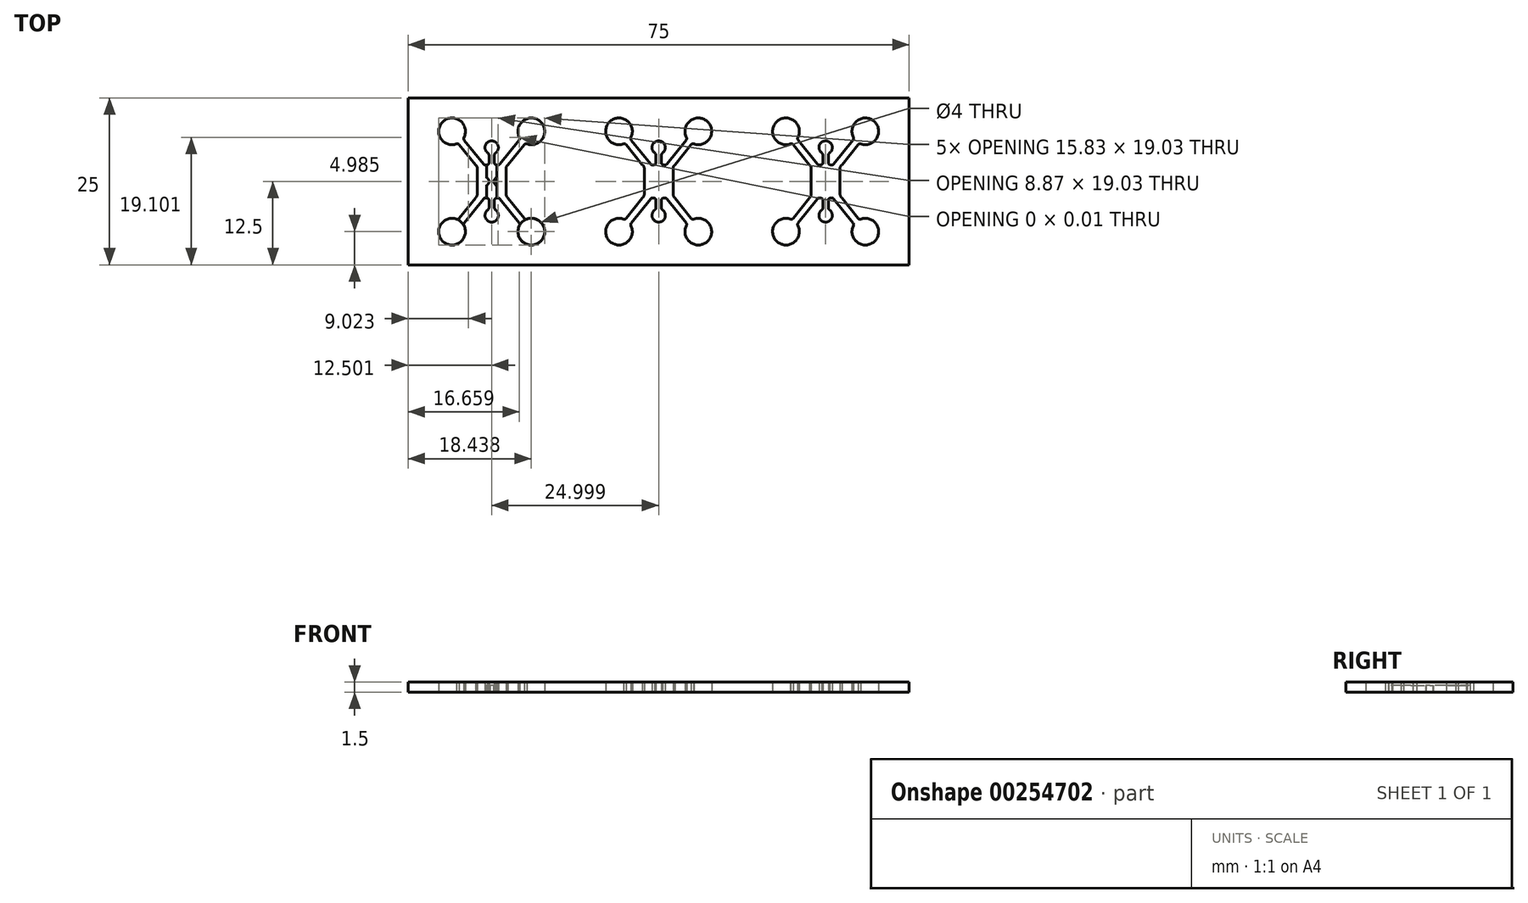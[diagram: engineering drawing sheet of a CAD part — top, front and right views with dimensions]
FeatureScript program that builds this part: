
annotation { "Feature Type Name" : "Feature", "Feature Type Description" : "" }
export const myFeature = defineFeature(function(context is Context, id is Id, definition is map)
    precondition{}
    {
        {
            var Q0;
            Q0=qCreatedBy(makeId("Top.planeOp"),FACE);
            var sketch = newSketch(context, id + "F0", { "sketchPlane" : qUnion([Q0])});
            skLineSegment(sketch, "E0.bottom", {"start": v(-37.5, 40) * mm, "end": v(37.5, 40) * mm});
            skLineSegment(sketch, "E0.top", {"start": v(-37.5, 15) * mm, "end": v(37.5, 15) * mm});
            skLineSegment(sketch, "E0.left", {"start": v(-37.5, 40) * mm, "end": v(-37.5, 15) * mm});
            skLineSegment(sketch, "E1.0", {"start": v(-37.5, 12.5) * mm, "end": v(37.5, 12.5) * mm});
            skLineSegment(sketch, "E2.top", {"start": v(-37.5, -12.5) * mm, "end": v(37.5, -12.5) * mm});
            skLineSegment(sketch, "E2.left", {"start": v(-37.5, 12.5) * mm, "end": v(-37.5, -12.5) * mm});
            skLineSegment(sketch, "E2.right", {"start": v(37.5, 12.5) * mm, "end": v(37.5, -12.5) * mm});
            skPoint(sketch, "E3.1.0.0", {"position": v(-17.06, 20.06) * mm});
            skPoint(sketch, "E3.1.0.4", {"position": v(-14.85, 26.8) * mm});
            skPoint(sketch, "E3.1.0.5", {"position": v(-25, 21.41) * mm});
            skLineSegment(sketch, "E3.1.0.10", {"start": v(-27.42, 30) * mm, "end": v(-29.86, 33.04) * mm});
            skPoint(sketch, "E3.1.0.11", {"position": v(-32.94, 20.06) * mm});
            skPoint(sketch, "E3.1.0.13", {"position": v(-25.75, 25) * mm});
            skPoint(sketch, "E3.1.0.15", {"position": v(-17.06, 34.94) * mm});
            skPoint(sketch, "E3.1.0.16", {"position": v(-24.49, 21.55) * mm});
            skLineSegment(sketch, "E3.1.0.17", {"start": v(-26.21, 24.92) * mm, "end": v(-29.12, 21.3) * mm});
            skLineSegment(sketch, "E3.1.0.19", {"start": v(-26.21, 30.08) * mm, "end": v(-29.1, 33.69) * mm});
            skLineSegment(sketch, "E3.1.0.20", {"start": v(-27.42, 25) * mm, "end": v(-29.87, 21.96) * mm});
            skPoint(sketch, "E3.1.0.24", {"position": v(-20.15, 29.65) * mm});
            skPoint(sketch, "E3.1.0.25", {"position": v(-22.85, 25.35) * mm});
            skPoint(sketch, "E3.1.0.27", {"position": v(-35.15, 26.8) * mm});
            skPoint(sketch, "E3.1.0.31", {"position": v(-27.15, 29.65) * mm});
            skPoint(sketch, "E3.1.0.35", {"position": v(-25.75, 30) * mm});
            skPoint(sketch, "E3.1.0.36", {"position": v(-27.15, 25.35) * mm});
            skPoint(sketch, "E3.1.0.41", {"position": v(-32.94, 34.94) * mm});
            skLineSegment(sketch, "E3.1.0.42", {"start": v(-23.79, 30.08) * mm, "end": v(-20.88, 33.7) * mm});
            skArc(sketch, "E3.1.0.43", {"start": v(-29.91, 29.7) * mm, "mid": v(-30, 29.78) * mm, "end": v(-30.1, 29.86) * mm});
            skArc(sketch, "E3.1.0.44", {"start": v(-20.08, 25.27) * mm, "mid": v(-14.77, 27.37) * mm, "end": v(-19.9, 29.89) * mm});
            skCircle(sketch, "E3.1.0.45", {"center": v(-19.06, 19.98) * mm, "radius": 2 * mm});
            skLineSegment(sketch, "E3.1.0.46", {"start": v(-23.79, 24.92) * mm, "end": v(-20.88, 21.3) * mm});
            skCircle(sketch, "E3.1.0.47", {"center": v(-30.94, 19.98) * mm, "radius": 2 * mm});
            skPoint(sketch, "E3.1.0.50", {"position": v(-25, 33.59) * mm});
            skLineSegment(sketch, "E3.1.0.60", {"start": v(-22.58, 25) * mm, "end": v(-20.13, 21.96) * mm});
            skPoint(sketch, "E3.1.0.61", {"position": v(-27.15, 25.35) * mm});
            skPoint(sketch, "E3.1.0.62", {"position": v(-27.15, 29.65) * mm});
            skPoint(sketch, "E3.1.0.64", {"position": v(-22.85, 25.35) * mm});
            skLineSegment(sketch, "E3.1.0.68", {"start": v(-22.58, 30) * mm, "end": v(-20.14, 33.04) * mm});
            skPoint(sketch, "E3.1.0.69", {"position": v(-27.15, 25.35) * mm});
            skPoint(sketch, "E3.1.0.72", {"position": v(-27.15, 29.65) * mm});
            skLineSegment(sketch, "E3.1.0.78", {"start": v(-29.85, 29.65) * mm, "end": v(-29.86, 29.65) * mm});
            skPoint(sketch, "E3.1.0.79", {"position": v(-22.85, 29.65) * mm});
            skPoint(sketch, "E3.1.0.81", {"position": v(-22.85, 25.35) * mm});
            skPoint(sketch, "E3.1.0.85", {"position": v(-22.85, 25.35) * mm});
            skPoint(sketch, "E3.1.0.87", {"position": v(-27.15, 25.35) * mm});
            skPoint(sketch, "E3.1.0.88", {"position": v(-27.15, 29.65) * mm});
            skLineSegment(sketch, "E3.1.0.89", {"start": v(-22.15, 29.65) * mm, "end": v(-20.49, 29.65) * mm});
            skPoint(sketch, "E3.1.0.90", {"position": v(-25, 27.5) * mm});
            skPoint(sketch, "E3.1.0.92", {"position": v(-22.85, 29.65) * mm});
            skPoint(sketch, "E3.1.0.95", {"position": v(-22.85, 25.35) * mm});
            skPoint(sketch, "E3.1.0.98", {"position": v(-27.15, 29.65) * mm});
            skPoint(sketch, "E3.1.0.99", {"position": v(-27.15, 25.35) * mm});
            skPoint(sketch, "E3.1.0.100", {"position": v(-22.85, 29.65) * mm});
            skLineSegment(sketch, "E3.1.0.104", {"start": v(-25.75, 25.21) * mm, "end": v(-25.75, 29.79) * mm});
            skLineSegment(sketch, "E3.1.0.105", {"start": v(-24.25, 29.79) * mm, "end": v(-24.25, 28.19) * mm});
            skLineSegment(sketch, "E3.1.0.106", {"start": v(-24.6, 24.7) * mm, "end": v(-24.6, 23.58) * mm});
            skLineSegment(sketch, "E3.1.0.108", {"start": v(-22.41, 29.65) * mm, "end": v(-22.15, 29.65) * mm});
            skLineSegment(sketch, "E3.1.0.109", {"start": v(-24.04, 30) * mm, "end": v(-23.95, 30) * mm});
            skLineSegment(sketch, "E3.1.0.110", {"start": v(-25.4, 30.5) * mm, "end": v(-25.4, 30.3) * mm});
            skArc(sketch, "E3.1.0.111", {"start": v(-24.6, 30.3) * mm, "mid": v(-24.51, 30.09) * mm, "end": v(-24.3, 30) * mm});
            skArc(sketch, "E3.1.0.112", {"start": v(-25.4, 30.3) * mm, "mid": v(-25.49, 30.09) * mm, "end": v(-25.7, 30) * mm});
            skLineSegment(sketch, "E3.1.0.113", {"start": v(-24.6, 30.3) * mm, "end": v(-24.6, 31.42) * mm});
            skLineSegment(sketch, "E3.1.0.115", {"start": v(-24.25, 30) * mm, "end": v(-24.3, 30) * mm});
            skLineSegment(sketch, "E3.1.0.117", {"start": v(-25.96, 30) * mm, "end": v(-26.05, 30) * mm});
            skLineSegment(sketch, "E3.1.0.118", {"start": v(-25.4, 24.7) * mm, "end": v(-25.4, 24.5) * mm});
            skLineSegment(sketch, "E3.1.0.120", {"start": v(-25.96, 25) * mm, "end": v(-26.05, 25) * mm});
            skArc(sketch, "E3.1.0.123", {"start": v(-25.4, 24.7) * mm, "mid": v(-25.49, 24.91) * mm, "end": v(-25.7, 25) * mm});
            skLineSegment(sketch, "E3.1.0.125", {"start": v(-24.25, 25) * mm, "end": v(-24.3, 25) * mm});
            skLineSegment(sketch, "E3.1.0.128", {"start": v(-24.04, 25) * mm, "end": v(-23.95, 25) * mm});
            skArc(sketch, "E3.1.0.134", {"start": v(-24.6, 24.7) * mm, "mid": v(-24.51, 24.91) * mm, "end": v(-24.3, 25) * mm});
            skLineSegment(sketch, "E3.1.0.151", {"start": v(-27.59, 25.35) * mm, "end": v(-27.85, 25.35) * mm});
            skLineSegment(sketch, "E4", {"start": v(-25.4, 24.5) * mm, "end": v(-25.4, 23.58) * mm});
            skLineSegment(sketch, "E5.top", {"start": v(-22.41, 25.35) * mm, "end": v(-20.5, 25.35) * mm});
            skLineSegment(sketch, "E5.left", {"start": v(-22.85, 29.44) * mm, "end": v(-22.85, 25.56) * mm});
            skLineSegment(sketch, "E5.right", {"start": v(-20.15, 29.57) * mm, "end": v(-20.15, 25.42) * mm});
            skLineSegment(sketch, "E6.right", {"start": v(-27.15, 29.44) * mm, "end": v(-27.15, 25.56) * mm});
            skLineSegment(sketch, "E7", {"start": v(-25.75, 25) * mm, "end": v(-25.7, 25) * mm});
            skLineSegment(sketch, "E8", {"start": v(-25.75, 30) * mm, "end": v(-25.7, 30) * mm});
            skLineSegment(sketch, "E9", {"start": v(-29.85, 25.35) * mm, "end": v(-29.85, 25.34) * mm});
            skArc(sketch, "E10.filletArc", {"start": v(-22.41, 25.35) * mm, "mid": v(-22.6, 25.23) * mm, "end": v(-22.58, 25) * mm});
            skPoint(sketch, "E11.visualSharp", {"position": v(-23.85, 25) * mm});
            skArc(sketch, "E11.filletArc", {"start": v(-23.79, 24.92) * mm, "mid": v(-23.86, 24.98) * mm, "end": v(-23.95, 25) * mm});
            skArc(sketch, "E12.filletArc", {"start": v(-22.58, 30) * mm, "mid": v(-22.6, 29.77) * mm, "end": v(-22.41, 29.65) * mm});
            skPoint(sketch, "E13.visualSharp", {"position": v(-23.85, 30) * mm});
            skArc(sketch, "E13.filletArc", {"start": v(-23.95, 30) * mm, "mid": v(-23.86, 30.02) * mm, "end": v(-23.79, 30.08) * mm});
            skPoint(sketch, "E14.visualSharp", {"position": v(-26.15, 30) * mm});
            skArc(sketch, "E14.filletArc", {"start": v(-26.21, 30.08) * mm, "mid": v(-26.14, 30.02) * mm, "end": v(-26.05, 30) * mm});
            skPoint(sketch, "E15.visualSharp", {"position": v(-26.15, 25) * mm});
            skArc(sketch, "E15.filletArc", {"start": v(-26.05, 25) * mm, "mid": v(-26.14, 24.98) * mm, "end": v(-26.21, 24.92) * mm});
            skArc(sketch, "E16", {"start": v(-27.42, 25) * mm, "mid": v(-27.26, 25.27) * mm, "end": v(-27.15, 25.56) * mm});
            skArc(sketch, "E17", {"start": v(-27.15, 29.44) * mm, "mid": v(-27.22, 29.75) * mm, "end": v(-27.42, 30) * mm});
            skArc(sketch, "E18", {"start": v(-27.59, 29.65) * mm, "mid": v(-27.43, 29.78) * mm, "end": v(-27.42, 30) * mm});
            skArc(sketch, "E19", {"start": v(-27.42, 25) * mm, "mid": v(-27.4, 25.23) * mm, "end": v(-27.59, 25.35) * mm});
            skArc(sketch, "E20.MirrorCS", {"start": v(-22.58, 25) * mm, "mid": v(-22.6, 25.23) * mm, "end": v(-22.41, 25.35) * mm});
            skArc(sketch, "E21.MirrorCS", {"start": v(-22.85, 29.44) * mm, "mid": v(-22.78, 29.75) * mm, "end": v(-22.58, 30) * mm});
            skArc(sketch, "E22.MirrorCS", {"start": v(-22.58, 25) * mm, "mid": v(-22.74, 25.27) * mm, "end": v(-22.85, 25.56) * mm});
            skLineSegment(sketch, "E23", {"start": v(-22.41, 29.65) * mm, "end": v(-20.49, 29.65) * mm});
            skArc(sketch, "E24", {"start": v(-19.9, 25.1) * mm, "mid": v(-20.18, 25.26) * mm, "end": v(-20.5, 25.35) * mm});
            skArc(sketch, "E25", {"start": v(-20.13, 21.96) * mm, "mid": v(-19.95, 21.86) * mm, "end": v(-19.75, 21.86) * mm});
            skArc(sketch, "E26", {"start": v(-20.85, 20.88) * mm, "mid": v(-20.81, 21.1) * mm, "end": v(-20.88, 21.3) * mm});
            skLineSegment(sketch, "E27", {"start": v(-24.6, 23.58) * mm, "end": v(-24.6, 23.58) * mm});
            skArc(sketch, "E28.MirrorCS", {"start": v(-29.87, 21.96) * mm, "mid": v(-30.05, 21.86) * mm, "end": v(-30.25, 21.86) * mm});
            skArc(sketch, "E29.MirrorCS", {"start": v(-29.15, 20.88) * mm, "mid": v(-29.19, 21.1) * mm, "end": v(-29.12, 21.3) * mm});
            skArc(sketch, "E30.MirrorCS", {"start": v(-25.4, 23.58) * mm, "mid": v(-25.46, 23.37) * mm, "end": v(-25.61, 23.2) * mm});
            skArc(sketch, "E31", {"start": v(-24.6, 23.58) * mm, "mid": v(-24.54, 23.37) * mm, "end": v(-24.39, 23.2) * mm});
            skArc(sketch, "E32", {"start": v(-25.61, 23.2) * mm, "mid": v(-25, 21.41) * mm, "end": v(-24.39, 23.2) * mm});
            skLineSegment(sketch, "E33", {"start": v(-29.12, 21.3) * mm, "end": v(-29.12, 21.3) * mm});
            skLineSegment(sketch, "E34", {"start": v(-29.5, 25.34) * mm, "end": v(-27.85, 25.35) * mm});
            skArc(sketch, "E35.filletArc", {"start": v(-29.91, 25.27) * mm, "mid": v(-29.87, 25.34) * mm, "end": v(-29.85, 25.42) * mm});
            skArc(sketch, "E36.filletArc", {"start": v(-29.85, 29.55) * mm, "mid": v(-29.87, 29.63) * mm, "end": v(-29.91, 29.7) * mm});
            skArc(sketch, "E37", {"start": v(-30.1, 29.86) * mm, "mid": v(-29.8, 29.72) * mm, "end": v(-29.5, 29.65) * mm});
            skArc(sketch, "E38", {"start": v(-30.27, 33.13) * mm, "mid": v(-32.26, 36.51) * mm, "end": v(-29.15, 34.12) * mm});
            skArc(sketch, "E39", {"start": v(-30.02, 33.24) * mm, "mid": v(-30.14, 33.18) * mm, "end": v(-30.27, 33.13) * mm});
            skArc(sketch, "E40", {"start": v(-29.15, 34.12) * mm, "mid": v(-29.52, 33.6) * mm, "end": v(-30.02, 33.24) * mm});
            skArc(sketch, "E41", {"start": v(-29.86, 33.04) * mm, "mid": v(-30.05, 33.13) * mm, "end": v(-30.27, 33.13) * mm});
            skArc(sketch, "E42", {"start": v(-29.15, 34.12) * mm, "mid": v(-29.19, 33.9) * mm, "end": v(-29.1, 33.69) * mm});
            skLineSegment(sketch, "E43", {"start": v(-25.4, 31.67) * mm, "end": v(-25.4, 31.67) * mm});
            skLineSegment(sketch, "E44", {"start": v(-25.4, 31.42) * mm, "end": v(-25.4, 30.5) * mm});
            skArc(sketch, "E45", {"start": v(-25.4, 31.42) * mm, "mid": v(-25.46, 31.64) * mm, "end": v(-25.62, 31.8) * mm});
            skArc(sketch, "E46", {"start": v(-24.38, 31.8) * mm, "mid": v(-25, 33.59) * mm, "end": v(-25.62, 31.8) * mm});
            skArc(sketch, "E47", {"start": v(-24.38, 31.8) * mm, "mid": v(-24.53, 31.64) * mm, "end": v(-24.6, 31.42) * mm});
            skArc(sketch, "E48.filletArc", {"start": v(-25.75, 29.79) * mm, "mid": v(-25.81, 29.94) * mm, "end": v(-25.96, 30) * mm});
            skLineSegment(sketch, "E49", {"start": v(-25.96, 30) * mm, "end": v(-25.75, 30) * mm});
            skPoint(sketch, "E50.visualSharp", {"position": v(-24.25, 30) * mm});
            skArc(sketch, "E50.filletArc", {"start": v(-24.04, 30) * mm, "mid": v(-24.19, 29.94) * mm, "end": v(-24.25, 29.79) * mm});
            skLineSegment(sketch, "E51", {"start": v(-24.25, 30) * mm, "end": v(-24.04, 30) * mm});
            skArc(sketch, "E52", {"start": v(-20.84, 34.1) * mm, "mid": v(-20.79, 34) * mm, "end": v(-20.72, 33.9) * mm});
            skArc(sketch, "E53", {"start": v(-20.72, 33.9) * mm, "mid": v(-20.4, 33.52) * mm, "end": v(-19.98, 33.24) * mm});
            skArc(sketch, "E54", {"start": v(-20.88, 33.7) * mm, "mid": v(-20.8, 33.9) * mm, "end": v(-20.84, 34.1) * mm});
            skArc(sketch, "E55", {"start": v(-19.73, 33.13) * mm, "mid": v(-17.75, 36.52) * mm, "end": v(-20.84, 34.1) * mm});
            skArc(sketch, "E56", {"start": v(-19.98, 33.24) * mm, "mid": v(-19.86, 33.18) * mm, "end": v(-19.73, 33.13) * mm});
            skArc(sketch, "E57", {"start": v(-19.73, 33.13) * mm, "mid": v(-19.94, 33.13) * mm, "end": v(-20.14, 33.04) * mm});
            skArc(sketch, "E58", {"start": v(-19.9, 29.89) * mm, "mid": v(-20, 29.8) * mm, "end": v(-20.08, 29.72) * mm});
            skLineSegment(sketch, "E59", {"start": v(-20.15, 29.65) * mm, "end": v(-20.15, 29.65) * mm});
            skArc(sketch, "E60", {"start": v(-20.49, 29.65) * mm, "mid": v(-20.18, 29.74) * mm, "end": v(-19.9, 29.89) * mm});
            skArc(sketch, "E61.filletArc", {"start": v(-20.08, 29.72) * mm, "mid": v(-20.13, 29.65) * mm, "end": v(-20.15, 29.57) * mm});
            skArc(sketch, "E62.filletArc", {"start": v(-20.15, 25.42) * mm, "mid": v(-20.13, 25.34) * mm, "end": v(-20.08, 25.27) * mm});
            skPoint(sketch, "E63.visualSharp", {"position": v(-24.25, 25) * mm});
            skArc(sketch, "E63.filletArc", {"start": v(-24.25, 25.21) * mm, "mid": v(-24.19, 25.06) * mm, "end": v(-24.04, 25) * mm});
            skLineSegment(sketch, "E64", {"start": v(-24.25, 25) * mm, "end": v(-24.04, 25) * mm});
            skLineSegment(sketch, "E65", {"start": v(-24.25, 25.21) * mm, "end": v(-24.25, 26.81) * mm});
            skArc(sketch, "E66.filletArc", {"start": v(-25.96, 25) * mm, "mid": v(-25.81, 25.06) * mm, "end": v(-25.75, 25.21) * mm});
            skLineSegment(sketch, "E67", {"start": v(-25.96, 25) * mm, "end": v(-25.75, 25) * mm});
            skArc(sketch, "E68", {"start": v(-30.1, 25.1) * mm, "mid": v(-30, 25.19) * mm, "end": v(-29.91, 25.27) * mm});
            skLineSegment(sketch, "E69", {"start": v(-29.91, 25.27) * mm, "end": v(-29.91, 25.27) * mm});
            skArc(sketch, "E70", {"start": v(-29.5, 25.34) * mm, "mid": v(-29.82, 25.26) * mm, "end": v(-30.1, 25.1) * mm});
            skLineSegment(sketch, "E71", {"start": v(-25, 32.59) * mm, "end": v(-25, 22.41) * mm});
            skPoint(sketch, "E72.endSnap0", {"position": v(-24.25, 27.5) * mm});
            skLineSegment(sketch, "E73", {"start": v(-24.72, 27.46) * mm, "end": v(-24.34, 26.96) * mm});
            skPoint(sketch, "E74.newPointB", {"position": v(-24.25, 25.21) * mm});
            skPoint(sketch, "E75.visualSharp", {"position": v(-24.75, 27.5) * mm});
            skArc(sketch, "E75.filletArc", {"start": v(-24.72, 27.54) * mm, "mid": v(-24.73, 27.52) * mm, "end": v(-24.73, 27.5) * mm});
            skArc(sketch, "E76.filletArc", {"start": v(-24.34, 26.96) * mm, "mid": v(-24.28, 26.94) * mm, "end": v(-24.25, 26.99) * mm});
            skLineSegment(sketch, "E77", {"start": v(-24.25, 27.5) * mm, "end": v(-24.25, 26.99) * mm});
            skArc(sketch, "E78", {"start": v(-24.73, 27.5) * mm, "mid": v(-24.73, 27.48) * mm, "end": v(-24.72, 27.46) * mm});
            skLineSegment(sketch, "E79.MirrorCS", {"start": v(-24.72, 27.54) * mm, "end": v(-24.34, 28.04) * mm});
            skArc(sketch, "E80.MirrorCS", {"start": v(-24.34, 28.04) * mm, "mid": v(-24.28, 28.06) * mm, "end": v(-24.25, 28.01) * mm});
            skLineSegment(sketch, "E81.MirrorCS", {"start": v(-24.25, 27.5) * mm, "end": v(-24.25, 28.01) * mm});
            skLineSegment(sketch, "E82", {"start": v(-24.25, 26.81) * mm, "end": v(-24.25, 26.99) * mm});
            skLineSegment(sketch, "E83", {"start": v(-24.25, 28.19) * mm, "end": v(-24.25, 28.01) * mm});
            skLineSegment(sketch, "E84.MirrorCS", {"start": v(-25.28, 27.54) * mm, "end": v(-25.66, 28.04) * mm});
            skArc(sketch, "E85.MirrorCS", {"start": v(-25.66, 28.04) * mm, "mid": v(-25.72, 28.06) * mm, "end": v(-25.75, 28.01) * mm});
            skArc(sketch, "E86.MirrorCS", {"start": v(-25.28, 27.54) * mm, "mid": v(-25.27, 27.52) * mm, "end": v(-25.27, 27.5) * mm});
            skArc(sketch, "E87.MirrorCS", {"start": v(-25.27, 27.5) * mm, "mid": v(-25.27, 27.48) * mm, "end": v(-25.28, 27.46) * mm});
            skLineSegment(sketch, "E88.MirrorCS", {"start": v(-25.28, 27.46) * mm, "end": v(-25.66, 26.96) * mm});
            skArc(sketch, "E89.MirrorCS", {"start": v(-25.66, 26.96) * mm, "mid": v(-25.72, 26.94) * mm, "end": v(-25.75, 26.99) * mm});
            skCircle(sketch, "E90", {"center": v(0, 13.86) * mm, "radius": 50 * mm});
            skLineSegment(sketch, "E91", {"start": v(37.5, 40) * mm, "end": v(37.5, 15) * mm});
            skPoint(sketch, "E92.1.0.0", {"position": v(7.94, 20.06) * mm});
            skPoint(sketch, "E92.1.0.1", {"position": v(0.51, 21.55) * mm});
            skPoint(sketch, "E92.1.0.2", {"position": v(7.94, 34.94) * mm});
            skPoint(sketch, "E92.1.0.3", {"position": v(0, 33.59) * mm});
            skPoint(sketch, "E92.1.0.4", {"position": v(-7.94, 20.06) * mm});
            skPoint(sketch, "E92.1.0.5", {"position": v(10.15, 26.8) * mm});
            skPoint(sketch, "E92.1.0.6", {"position": v(-7.94, 34.94) * mm});
            skArc(sketch, "E92.1.0.7", {"start": v(4.92, 25.27) * mm, "mid": v(10.23, 27.37) * mm, "end": v(5.1, 29.89) * mm});
            skPoint(sketch, "E92.1.0.8", {"position": v(-2.15, 25.35) * mm});
            skPoint(sketch, "E92.1.0.9", {"position": v(0, 21.41) * mm});
            skArc(sketch, "E92.1.0.10", {"start": v(-5.1, 29.86) * mm, "mid": v(-10.1, 27.5) * mm, "end": v(-5.1, 25.1) * mm});
            skCircle(sketch, "E92.1.0.11", {"center": v(-5.94, 19.98) * mm, "radius": 2 * mm});
            skPoint(sketch, "E92.1.0.12", {"position": v(0.75, 30) * mm});
            skPoint(sketch, "E92.1.0.13", {"position": v(1.15, 25) * mm});
            skPoint(sketch, "E92.1.0.14", {"position": v(-2.15, 29.65) * mm});
            skCircle(sketch, "E92.1.0.15", {"center": v(5.94, 19.98) * mm, "radius": 2 * mm});
            skPoint(sketch, "E92.1.0.16", {"position": v(-0.75, 25) * mm});
            skPoint(sketch, "E92.1.0.17", {"position": v(2.15, 25.35) * mm});
            skPoint(sketch, "E92.1.0.18", {"position": v(-2.15, 25.35) * mm});
            skPoint(sketch, "E92.1.0.19", {"position": v(4.85, 29.65) * mm});
            skPoint(sketch, "E92.1.0.20", {"position": v(-0.75, 25) * mm});
            skPoint(sketch, "E92.1.0.21", {"position": v(2.15, 25.35) * mm});
            skPoint(sketch, "E92.1.0.22", {"position": v(-2.15, 29.65) * mm});
            skPoint(sketch, "E92.1.0.23", {"position": v(2.15, 29.65) * mm});
            skPoint(sketch, "E92.1.0.24", {"position": v(-0.75, 30) * mm});
            skLineSegment(sketch, "E92.1.0.25", {"start": v(1.21, 24.92) * mm, "end": v(4.12, 21.3) * mm});
            skPoint(sketch, "E92.1.0.26", {"position": v(2.15, 29.65) * mm});
            skLineSegment(sketch, "E92.1.0.27", {"start": v(2.42, 25) * mm, "end": v(4.87, 21.96) * mm});
            skArc(sketch, "E92.1.0.28", {"start": v(4.15, 20.88) * mm, "mid": v(4.19, 21.1) * mm, "end": v(4.12, 21.3) * mm});
            skArc(sketch, "E92.1.0.29", {"start": v(-5.27, 33.13) * mm, "mid": v(-7.26, 36.51) * mm, "end": v(-4.15, 34.12) * mm});
            skPoint(sketch, "E92.1.0.30", {"position": v(-2.15, 25.35) * mm});
            skPoint(sketch, "E92.1.0.31", {"position": v(2.15, 25.35) * mm});
            skPoint(sketch, "E92.1.0.32", {"position": v(-2.15, 29.65) * mm});
            skPoint(sketch, "E92.1.0.33", {"position": v(-1.15, 30) * mm});
            skPoint(sketch, "E92.1.0.34", {"position": v(-1.15, 25) * mm});
            skPoint(sketch, "E92.1.0.35", {"position": v(1.15, 30) * mm});
            skArc(sketch, "E92.1.0.36", {"start": v(4.87, 21.96) * mm, "mid": v(5.05, 21.86) * mm, "end": v(5.25, 21.86) * mm});
            skPoint(sketch, "E92.1.0.37", {"position": v(2.15, 25.35) * mm});
            skArc(sketch, "E92.1.0.38", {"start": v(5.27, 33.13) * mm, "mid": v(7.25, 36.52) * mm, "end": v(4.16, 34.1) * mm});
            skPoint(sketch, "E92.1.0.39", {"position": v(-2.15, 25.35) * mm});
            skPoint(sketch, "E92.1.0.40", {"position": v(2.15, 29.65) * mm});
            skPoint(sketch, "E92.1.0.41", {"position": v(-2.15, 29.65) * mm});
            skPoint(sketch, "E92.1.0.42", {"position": v(-2.15, 29.65) * mm});
            skPoint(sketch, "E92.1.0.43", {"position": v(2.15, 25.35) * mm});
            skPoint(sketch, "E92.1.0.44", {"position": v(-2.15, 25.35) * mm});
            skPoint(sketch, "E92.1.0.45", {"position": v(2.15, 29.65) * mm});
            skPoint(sketch, "E92.1.0.46", {"position": v(0.75, 25) * mm});
            skPoint(sketch, "E92.1.0.47", {"position": v(0.25, 27.5) * mm});
            skArc(sketch, "E92.1.0.48", {"start": v(0.62, 31.8) * mm, "mid": v(0, 33.59) * mm, "end": v(-0.62, 31.8) * mm});
            skPoint(sketch, "E92.1.0.49", {"position": v(2.15, 25.35) * mm});
            skArc(sketch, "E92.1.0.50", {"start": v(-0.61, 23.2) * mm, "mid": v(0, 21.41) * mm, "end": v(0.61, 23.2) * mm});
            skLineSegment(sketch, "E92.1.0.51", {"start": v(-1.21, 24.92) * mm, "end": v(-4.12, 21.3) * mm});
            skPoint(sketch, "E92.1.0.52", {"position": v(0.75, 27.5) * mm});
            skLineSegment(sketch, "E92.1.0.53", {"start": v(-2.42, 25) * mm, "end": v(-4.87, 21.96) * mm});
            skPoint(sketch, "E92.1.0.54", {"position": v(0.75, 25.21) * mm});
            skPoint(sketch, "E92.1.0.55", {"position": v(-2.15, 25.35) * mm});
            skPoint(sketch, "E92.1.0.56", {"position": v(2.15, 29.65) * mm});
            skPoint(sketch, "E92.1.0.57", {"position": v(-2.15, 29.65) * mm});
            skPoint(sketch, "E92.1.0.58", {"position": v(0, 27.5) * mm});
            skArc(sketch, "E92.1.0.59", {"start": v(-4.87, 21.96) * mm, "mid": v(-5.05, 21.86) * mm, "end": v(-5.25, 21.86) * mm});
            skLineSegment(sketch, "E92.1.0.60", {"start": v(2.42, 30) * mm, "end": v(4.86, 33.04) * mm});
            skArc(sketch, "E92.1.0.61", {"start": v(-4.15, 34.12) * mm, "mid": v(-4.52, 33.6) * mm, "end": v(-5.02, 33.24) * mm});
            skArc(sketch, "E92.1.0.62", {"start": v(-4.86, 33.04) * mm, "mid": v(-5.05, 33.13) * mm, "end": v(-5.27, 33.13) * mm});
            skPoint(sketch, "E92.1.0.63", {"position": v(-0.75, 30) * mm});
            skArc(sketch, "E92.1.0.64", {"start": v(-4.15, 34.12) * mm, "mid": v(-4.19, 33.9) * mm, "end": v(-4.1, 33.69) * mm});
            skLineSegment(sketch, "E92.1.0.65", {"start": v(1.21, 30.08) * mm, "end": v(4.12, 33.7) * mm});
            skLineSegment(sketch, "E92.1.0.66", {"start": v(-2.42, 30) * mm, "end": v(-4.86, 33.04) * mm});
            skLineSegment(sketch, "E92.1.0.67", {"start": v(-1.21, 30.08) * mm, "end": v(-4.1, 33.69) * mm});
            skArc(sketch, "E92.1.0.68", {"start": v(4.28, 33.9) * mm, "mid": v(4.6, 33.52) * mm, "end": v(5.02, 33.24) * mm});
            skPoint(sketch, "E92.1.0.69", {"position": v(2.15, 25.35) * mm});
            skArc(sketch, "E92.1.0.70", {"start": v(-4.15, 20.88) * mm, "mid": v(-4.19, 21.1) * mm, "end": v(-4.12, 21.3) * mm});
            skArc(sketch, "E92.1.0.71", {"start": v(5.27, 33.13) * mm, "mid": v(5.06, 33.13) * mm, "end": v(4.86, 33.04) * mm});
            skPoint(sketch, "E92.1.0.72", {"position": v(-2.15, 25.35) * mm});
            skLineSegment(sketch, "E92.1.0.73", {"start": v(4.85, 29.57) * mm, "end": v(4.85, 25.42) * mm});
            skArc(sketch, "E92.1.0.74", {"start": v(4.12, 33.7) * mm, "mid": v(4.2, 33.9) * mm, "end": v(4.16, 34.1) * mm});
            skArc(sketch, "E92.1.0.75", {"start": v(5.1, 25.1) * mm, "mid": v(4.82, 25.26) * mm, "end": v(4.5, 25.35) * mm});
            skArc(sketch, "E92.1.0.76", {"start": v(-5.02, 33.24) * mm, "mid": v(-5.14, 33.18) * mm, "end": v(-5.27, 33.13) * mm});
            skArc(sketch, "E92.1.0.77", {"start": v(5.02, 33.24) * mm, "mid": v(5.14, 33.18) * mm, "end": v(5.27, 33.13) * mm});
            skArc(sketch, "E92.1.0.78", {"start": v(4.85, 25.42) * mm, "mid": v(4.87, 25.34) * mm, "end": v(4.92, 25.27) * mm});
            skArc(sketch, "E92.1.0.79", {"start": v(4.16, 34.1) * mm, "mid": v(4.21, 34) * mm, "end": v(4.28, 33.9) * mm});
            skLineSegment(sketch, "E92.1.0.80", {"start": v(-4.85, 29.55) * mm, "end": v(-4.85, 25.42) * mm});
            skArc(sketch, "E92.1.0.81", {"start": v(-4.91, 29.7) * mm, "mid": v(-5, 29.78) * mm, "end": v(-5.1, 29.86) * mm});
            skLineSegment(sketch, "E92.1.0.82", {"start": v(-4.85, 25.35) * mm, "end": v(-4.85, 25.34) * mm});
            skArc(sketch, "E92.1.0.83", {"start": v(-4.5, 25.34) * mm, "mid": v(-4.82, 25.26) * mm, "end": v(-5.1, 25.1) * mm});
            skArc(sketch, "E92.1.0.84", {"start": v(-5.1, 29.86) * mm, "mid": v(-4.8, 29.72) * mm, "end": v(-4.5, 29.65) * mm});
            skArc(sketch, "E92.1.0.85", {"start": v(-4.85, 29.55) * mm, "mid": v(-4.87, 29.63) * mm, "end": v(-4.91, 29.7) * mm});
            skArc(sketch, "E92.1.0.86", {"start": v(-5.1, 25.1) * mm, "mid": v(-5, 25.19) * mm, "end": v(-4.91, 25.27) * mm});
            skArc(sketch, "E92.1.0.87", {"start": v(4.51, 29.65) * mm, "mid": v(4.82, 29.74) * mm, "end": v(5.1, 29.89) * mm});
            skArc(sketch, "E92.1.0.88", {"start": v(5.1, 29.89) * mm, "mid": v(5, 29.8) * mm, "end": v(4.92, 29.72) * mm});
            skLineSegment(sketch, "E92.1.0.89", {"start": v(-4.85, 29.65) * mm, "end": v(-4.86, 29.65) * mm});
            skArc(sketch, "E92.1.0.90", {"start": v(-4.91, 25.27) * mm, "mid": v(-4.87, 25.34) * mm, "end": v(-4.85, 25.42) * mm});
            skLineSegment(sketch, "E92.1.0.91", {"start": v(0, 32.59) * mm, "end": v(0, 22.41) * mm});
            skArc(sketch, "E92.1.0.92", {"start": v(4.92, 29.72) * mm, "mid": v(4.87, 29.65) * mm, "end": v(4.85, 29.57) * mm});
            skLineSegment(sketch, "E92.1.0.93", {"start": v(-4.5, 25.34) * mm, "end": v(-2.85, 25.35) * mm});
            skLineSegment(sketch, "E92.1.0.94", {"start": v(-4.5, 29.65) * mm, "end": v(-2.59, 29.65) * mm});
            skLineSegment(sketch, "E92.1.0.95", {"start": v(2.59, 29.65) * mm, "end": v(4.51, 29.65) * mm});
            skLineSegment(sketch, "E92.1.0.96", {"start": v(2.59, 25.35) * mm, "end": v(4.5, 25.35) * mm});
            skLineSegment(sketch, "E92.1.0.97", {"start": v(2.85, 29.65) * mm, "end": v(4.51, 29.65) * mm});
            skArc(sketch, "E92.1.0.98", {"start": v(-2.15, 29.44) * mm, "mid": v(-2.22, 29.75) * mm, "end": v(-2.42, 30) * mm});
            skArc(sketch, "E92.1.0.99", {"start": v(-2.59, 29.65) * mm, "mid": v(-2.43, 29.78) * mm, "end": v(-2.42, 30) * mm});
            skArc(sketch, "E92.1.0.100", {"start": v(-0.4, 31.42) * mm, "mid": v(-0.46, 31.64) * mm, "end": v(-0.62, 31.8) * mm});
            skLineSegment(sketch, "E92.1.0.101", {"start": v(0.4, 30.3) * mm, "end": v(0.4, 31.42) * mm});
            skLineSegment(sketch, "E92.1.0.102", {"start": v(-0.4, 31.42) * mm, "end": v(-0.4, 30.5) * mm});
            skLineSegment(sketch, "E92.1.0.103", {"start": v(-2.15, 29.44) * mm, "end": v(-2.15, 25.56) * mm});
            skArc(sketch, "E92.1.0.104", {"start": v(0.62, 31.8) * mm, "mid": v(0.47, 31.64) * mm, "end": v(0.4, 31.42) * mm});
            skLineSegment(sketch, "E92.1.0.105", {"start": v(0.75, 30) * mm, "end": v(0.7, 30) * mm});
            skLineSegment(sketch, "E92.1.0.106", {"start": v(2.59, 29.65) * mm, "end": v(2.85, 29.65) * mm});
            skArc(sketch, "E92.1.0.107", {"start": v(2.15, 29.44) * mm, "mid": v(2.22, 29.75) * mm, "end": v(2.42, 30) * mm});
            skLineSegment(sketch, "E92.1.0.108", {"start": v(-0.96, 30) * mm, "end": v(-1.05, 30) * mm});
            skLineSegment(sketch, "E92.1.0.109", {"start": v(-0.75, 30) * mm, "end": v(-0.7, 30) * mm});
            skArc(sketch, "E92.1.0.110", {"start": v(-2.42, 25) * mm, "mid": v(-2.4, 25.23) * mm, "end": v(-2.59, 25.35) * mm});
            skArc(sketch, "E92.1.0.111", {"start": v(-2.42, 25) * mm, "mid": v(-2.26, 25.27) * mm, "end": v(-2.15, 25.56) * mm});
            skArc(sketch, "E92.1.0.112", {"start": v(-0.4, 30.3) * mm, "mid": v(-0.49, 30.09) * mm, "end": v(-0.7, 30) * mm});
            skLineSegment(sketch, "E92.1.0.113", {"start": v(0.75, 29.79) * mm, "end": v(0.75, 28.19) * mm});
            skArc(sketch, "E92.1.0.114", {"start": v(0.96, 30) * mm, "mid": v(0.81, 29.94) * mm, "end": v(0.75, 29.79) * mm});
            skLineSegment(sketch, "E92.1.0.115", {"start": v(0.28, 27.54) * mm, "end": v(0.66, 28.04) * mm});
            skArc(sketch, "E92.1.0.116", {"start": v(-0.27, 27.5) * mm, "mid": v(-0.27, 27.48) * mm, "end": v(-0.28, 27.46) * mm});
            skLineSegment(sketch, "E92.1.0.117", {"start": v(0.75, 30) * mm, "end": v(0.96, 30) * mm});
            skLineSegment(sketch, "E92.1.0.118", {"start": v(-0.96, 30) * mm, "end": v(-0.75, 30) * mm});
            skArc(sketch, "E92.1.0.119", {"start": v(2.42, 30) * mm, "mid": v(2.4, 29.77) * mm, "end": v(2.59, 29.65) * mm});
            skArc(sketch, "E92.1.0.120", {"start": v(0.4, 30.3) * mm, "mid": v(0.49, 30.09) * mm, "end": v(0.7, 30) * mm});
            skLineSegment(sketch, "E92.1.0.121", {"start": v(-0.75, 25.21) * mm, "end": v(-0.75, 29.79) * mm});
            skArc(sketch, "E92.1.0.122", {"start": v(-0.75, 29.79) * mm, "mid": v(-0.81, 29.94) * mm, "end": v(-0.96, 30) * mm});
            skLineSegment(sketch, "E92.1.0.123", {"start": v(2.15, 29.44) * mm, "end": v(2.15, 25.56) * mm});
            skLineSegment(sketch, "E92.1.0.124", {"start": v(0.75, 27.5) * mm, "end": v(0.75, 26.99) * mm});
            skArc(sketch, "E92.1.0.125", {"start": v(2.42, 25) * mm, "mid": v(2.26, 25.27) * mm, "end": v(2.15, 25.56) * mm});
            skLineSegment(sketch, "E92.1.0.126", {"start": v(-0.4, 24.5) * mm, "end": v(-0.4, 23.58) * mm});
            skArc(sketch, "E92.1.0.127", {"start": v(-0.96, 25) * mm, "mid": v(-0.81, 25.06) * mm, "end": v(-0.75, 25.21) * mm});
            skLineSegment(sketch, "E92.1.0.128", {"start": v(0.75, 25.21) * mm, "end": v(0.75, 26.81) * mm});
            skLineSegment(sketch, "E92.1.0.129", {"start": v(-2.59, 25.35) * mm, "end": v(-2.85, 25.35) * mm});
            skLineSegment(sketch, "E92.1.0.130", {"start": v(-0.4, 30.5) * mm, "end": v(-0.4, 30.3) * mm});
            skArc(sketch, "E92.1.0.131", {"start": v(2.59, 25.35) * mm, "mid": v(2.4, 25.23) * mm, "end": v(2.42, 25) * mm});
            skLineSegment(sketch, "E92.1.0.132", {"start": v(0.96, 30) * mm, "end": v(1.05, 30) * mm});
            skLineSegment(sketch, "E92.1.0.133", {"start": v(0.4, 24.7) * mm, "end": v(0.4, 23.58) * mm});
            skLineSegment(sketch, "E92.1.0.134", {"start": v(0.75, 28.19) * mm, "end": v(0.75, 28.01) * mm});
            skLineSegment(sketch, "E92.1.0.135", {"start": v(-0.96, 25) * mm, "end": v(-1.05, 25) * mm});
            skArc(sketch, "E92.1.0.136", {"start": v(-0.66, 26.96) * mm, "mid": v(-0.72, 26.94) * mm, "end": v(-0.75, 26.99) * mm});
            skArc(sketch, "E92.1.0.137", {"start": v(-0.28, 27.54) * mm, "mid": v(-0.27, 27.52) * mm, "end": v(-0.27, 27.5) * mm});
            skLineSegment(sketch, "E92.1.0.138", {"start": v(-0.4, 24.7) * mm, "end": v(-0.4, 24.5) * mm});
            skArc(sketch, "E92.1.0.139", {"start": v(0.27, 27.5) * mm, "mid": v(0.27, 27.48) * mm, "end": v(0.28, 27.46) * mm});
            skArc(sketch, "E92.1.0.140", {"start": v(0.66, 26.96) * mm, "mid": v(0.72, 26.94) * mm, "end": v(0.75, 26.99) * mm});
            skArc(sketch, "E92.1.0.141", {"start": v(-1.21, 30.08) * mm, "mid": v(-1.14, 30.02) * mm, "end": v(-1.05, 30) * mm});
            skArc(sketch, "E92.1.0.142", {"start": v(1.21, 24.92) * mm, "mid": v(1.14, 24.98) * mm, "end": v(1.05, 25) * mm});
            skArc(sketch, "E92.1.0.143", {"start": v(-0.66, 28.04) * mm, "mid": v(-0.72, 28.06) * mm, "end": v(-0.75, 28.01) * mm});
            skLineSegment(sketch, "E92.1.0.144", {"start": v(-0.28, 27.46) * mm, "end": v(-0.66, 26.96) * mm});
            skArc(sketch, "E92.1.0.145", {"start": v(0.28, 27.54) * mm, "mid": v(0.27, 27.52) * mm, "end": v(0.27, 27.5) * mm});
            skLineSegment(sketch, "E92.1.0.146", {"start": v(0.28, 27.46) * mm, "end": v(0.66, 26.96) * mm});
            skArc(sketch, "E92.1.0.147", {"start": v(2.42, 25) * mm, "mid": v(2.4, 25.23) * mm, "end": v(2.59, 25.35) * mm});
            skArc(sketch, "E92.1.0.148", {"start": v(0.4, 24.7) * mm, "mid": v(0.49, 24.91) * mm, "end": v(0.7, 25) * mm});
            skLineSegment(sketch, "E92.1.0.149", {"start": v(0.75, 26.81) * mm, "end": v(0.75, 26.99) * mm});
            skArc(sketch, "E92.1.0.150", {"start": v(-0.4, 23.58) * mm, "mid": v(-0.46, 23.37) * mm, "end": v(-0.61, 23.2) * mm});
            skArc(sketch, "E92.1.0.151", {"start": v(1.05, 30) * mm, "mid": v(1.14, 30.02) * mm, "end": v(1.21, 30.08) * mm});
            skLineSegment(sketch, "E92.1.0.152", {"start": v(-0.75, 25) * mm, "end": v(-0.7, 25) * mm});
            skLineSegment(sketch, "E92.1.0.153", {"start": v(0.75, 25) * mm, "end": v(0.96, 25) * mm});
            skLineSegment(sketch, "E92.1.0.154", {"start": v(-0.96, 25) * mm, "end": v(-0.75, 25) * mm});
            skArc(sketch, "E92.1.0.155", {"start": v(0.75, 25.21) * mm, "mid": v(0.81, 25.06) * mm, "end": v(0.96, 25) * mm});
            skArc(sketch, "E92.1.0.156", {"start": v(0.4, 23.58) * mm, "mid": v(0.46, 23.37) * mm, "end": v(0.61, 23.2) * mm});
            skLineSegment(sketch, "E92.1.0.157", {"start": v(0.75, 27.5) * mm, "end": v(0.75, 28.01) * mm});
            skLineSegment(sketch, "E92.1.0.158", {"start": v(0.96, 25) * mm, "end": v(1.05, 25) * mm});
            skArc(sketch, "E92.1.0.159", {"start": v(-0.4, 23.58) * mm, "mid": v(-0.46, 23.37) * mm, "end": v(-0.61, 23.2) * mm});
            skArc(sketch, "E92.1.0.160", {"start": v(0.66, 28.04) * mm, "mid": v(0.72, 28.06) * mm, "end": v(0.75, 28.01) * mm});
            skLineSegment(sketch, "E92.1.0.161", {"start": v(0.75, 25) * mm, "end": v(0.7, 25) * mm});
            skLineSegment(sketch, "E92.1.0.162", {"start": v(-0.28, 27.54) * mm, "end": v(-0.66, 28.04) * mm});
            skArc(sketch, "E92.1.0.163", {"start": v(-0.4, 24.7) * mm, "mid": v(-0.49, 24.91) * mm, "end": v(-0.7, 25) * mm});
            skArc(sketch, "E92.1.0.164", {"start": v(-1.05, 25) * mm, "mid": v(-1.14, 24.98) * mm, "end": v(-1.21, 24.92) * mm});
            skPoint(sketch, "E92.2.0.0", {"position": v(32.94, 20.06) * mm});
            skPoint(sketch, "E92.2.0.1", {"position": v(25.51, 21.55) * mm});
            skPoint(sketch, "E92.2.0.2", {"position": v(32.94, 34.94) * mm});
            skPoint(sketch, "E92.2.0.3", {"position": v(25, 33.59) * mm});
            skPoint(sketch, "E92.2.0.4", {"position": v(17.06, 20.06) * mm});
            skPoint(sketch, "E92.2.0.5", {"position": v(35.15, 26.8) * mm});
            skPoint(sketch, "E92.2.0.6", {"position": v(17.06, 34.94) * mm});
            skArc(sketch, "E92.2.0.7", {"start": v(29.92, 25.27) * mm, "mid": v(35.23, 27.37) * mm, "end": v(30.1, 29.89) * mm});
            skPoint(sketch, "E92.2.0.8", {"position": v(22.85, 25.35) * mm});
            skPoint(sketch, "E92.2.0.9", {"position": v(25, 21.41) * mm});
            skArc(sketch, "E92.2.0.10", {"start": v(19.9, 29.86) * mm, "mid": v(14.9, 27.5) * mm, "end": v(19.9, 25.1) * mm});
            skCircle(sketch, "E92.2.0.11", {"center": v(19.06, 19.98) * mm, "radius": 2 * mm});
            skPoint(sketch, "E92.2.0.12", {"position": v(25.75, 30) * mm});
            skPoint(sketch, "E92.2.0.13", {"position": v(26.15, 25) * mm});
            skPoint(sketch, "E92.2.0.14", {"position": v(22.85, 29.65) * mm});
            skCircle(sketch, "E92.2.0.15", {"center": v(30.94, 19.98) * mm, "radius": 2 * mm});
            skPoint(sketch, "E92.2.0.16", {"position": v(24.25, 25) * mm});
            skPoint(sketch, "E92.2.0.17", {"position": v(27.15, 25.35) * mm});
            skPoint(sketch, "E92.2.0.18", {"position": v(22.85, 25.35) * mm});
            skPoint(sketch, "E92.2.0.19", {"position": v(29.85, 29.65) * mm});
            skPoint(sketch, "E92.2.0.20", {"position": v(24.25, 25) * mm});
            skPoint(sketch, "E92.2.0.21", {"position": v(27.15, 25.35) * mm});
            skPoint(sketch, "E92.2.0.22", {"position": v(22.85, 29.65) * mm});
            skPoint(sketch, "E92.2.0.23", {"position": v(27.15, 29.65) * mm});
            skPoint(sketch, "E92.2.0.24", {"position": v(24.25, 30) * mm});
            skLineSegment(sketch, "E92.2.0.25", {"start": v(26.21, 24.92) * mm, "end": v(29.12, 21.3) * mm});
            skPoint(sketch, "E92.2.0.26", {"position": v(27.15, 29.65) * mm});
            skLineSegment(sketch, "E92.2.0.27", {"start": v(27.42, 25) * mm, "end": v(29.87, 21.96) * mm});
            skArc(sketch, "E92.2.0.28", {"start": v(29.15, 20.88) * mm, "mid": v(29.19, 21.1) * mm, "end": v(29.12, 21.3) * mm});
            skArc(sketch, "E92.2.0.29", {"start": v(19.73, 33.13) * mm, "mid": v(17.74, 36.51) * mm, "end": v(20.85, 34.12) * mm});
            skPoint(sketch, "E92.2.0.30", {"position": v(22.85, 25.35) * mm});
            skPoint(sketch, "E92.2.0.31", {"position": v(27.15, 25.35) * mm});
            skPoint(sketch, "E92.2.0.32", {"position": v(22.85, 29.65) * mm});
            skPoint(sketch, "E92.2.0.33", {"position": v(23.85, 30) * mm});
            skPoint(sketch, "E92.2.0.34", {"position": v(23.85, 25) * mm});
            skPoint(sketch, "E92.2.0.35", {"position": v(26.15, 30) * mm});
            skArc(sketch, "E92.2.0.36", {"start": v(29.87, 21.96) * mm, "mid": v(30.05, 21.86) * mm, "end": v(30.25, 21.86) * mm});
            skPoint(sketch, "E92.2.0.37", {"position": v(27.15, 25.35) * mm});
            skArc(sketch, "E92.2.0.38", {"start": v(30.27, 33.13) * mm, "mid": v(32.25, 36.52) * mm, "end": v(29.16, 34.1) * mm});
            skPoint(sketch, "E92.2.0.39", {"position": v(22.85, 25.35) * mm});
            skPoint(sketch, "E92.2.0.40", {"position": v(27.15, 29.65) * mm});
            skPoint(sketch, "E92.2.0.41", {"position": v(22.85, 29.65) * mm});
            skPoint(sketch, "E92.2.0.42", {"position": v(22.85, 29.65) * mm});
            skPoint(sketch, "E92.2.0.43", {"position": v(27.15, 25.35) * mm});
            skPoint(sketch, "E92.2.0.44", {"position": v(22.85, 25.35) * mm});
            skPoint(sketch, "E92.2.0.45", {"position": v(27.15, 29.65) * mm});
            skPoint(sketch, "E92.2.0.46", {"position": v(25.75, 25) * mm});
            skPoint(sketch, "E92.2.0.47", {"position": v(25.25, 27.5) * mm});
            skArc(sketch, "E92.2.0.48", {"start": v(25.62, 31.8) * mm, "mid": v(25, 33.59) * mm, "end": v(24.38, 31.8) * mm});
            skPoint(sketch, "E92.2.0.49", {"position": v(27.15, 25.35) * mm});
            skArc(sketch, "E92.2.0.50", {"start": v(24.39, 23.2) * mm, "mid": v(25, 21.41) * mm, "end": v(25.61, 23.2) * mm});
            skLineSegment(sketch, "E92.2.0.51", {"start": v(23.79, 24.92) * mm, "end": v(20.88, 21.3) * mm});
            skPoint(sketch, "E92.2.0.52", {"position": v(25.75, 27.5) * mm});
            skLineSegment(sketch, "E92.2.0.53", {"start": v(22.58, 25) * mm, "end": v(20.13, 21.96) * mm});
            skPoint(sketch, "E92.2.0.54", {"position": v(25.75, 25.21) * mm});
            skPoint(sketch, "E92.2.0.55", {"position": v(22.85, 25.35) * mm});
            skPoint(sketch, "E92.2.0.56", {"position": v(27.15, 29.65) * mm});
            skPoint(sketch, "E92.2.0.57", {"position": v(22.85, 29.65) * mm});
            skPoint(sketch, "E92.2.0.58", {"position": v(25, 27.5) * mm});
            skArc(sketch, "E92.2.0.59", {"start": v(20.13, 21.96) * mm, "mid": v(19.95, 21.86) * mm, "end": v(19.75, 21.86) * mm});
            skLineSegment(sketch, "E92.2.0.60", {"start": v(27.42, 30) * mm, "end": v(29.86, 33.04) * mm});
            skArc(sketch, "E92.2.0.61", {"start": v(20.85, 34.12) * mm, "mid": v(20.48, 33.6) * mm, "end": v(19.98, 33.24) * mm});
            skArc(sketch, "E92.2.0.62", {"start": v(20.14, 33.04) * mm, "mid": v(19.95, 33.13) * mm, "end": v(19.73, 33.13) * mm});
            skPoint(sketch, "E92.2.0.63", {"position": v(24.25, 30) * mm});
            skArc(sketch, "E92.2.0.64", {"start": v(20.85, 34.12) * mm, "mid": v(20.81, 33.9) * mm, "end": v(20.9, 33.69) * mm});
            skLineSegment(sketch, "E92.2.0.65", {"start": v(26.21, 30.08) * mm, "end": v(29.12, 33.7) * mm});
            skLineSegment(sketch, "E92.2.0.66", {"start": v(22.58, 30) * mm, "end": v(20.14, 33.04) * mm});
            skLineSegment(sketch, "E92.2.0.67", {"start": v(23.79, 30.08) * mm, "end": v(20.9, 33.69) * mm});
            skArc(sketch, "E92.2.0.68", {"start": v(29.28, 33.9) * mm, "mid": v(29.6, 33.52) * mm, "end": v(30.02, 33.24) * mm});
            skPoint(sketch, "E92.2.0.69", {"position": v(27.15, 25.35) * mm});
            skArc(sketch, "E92.2.0.70", {"start": v(20.85, 20.88) * mm, "mid": v(20.81, 21.1) * mm, "end": v(20.88, 21.3) * mm});
            skArc(sketch, "E92.2.0.71", {"start": v(30.27, 33.13) * mm, "mid": v(30.06, 33.13) * mm, "end": v(29.86, 33.04) * mm});
            skPoint(sketch, "E92.2.0.72", {"position": v(22.85, 25.35) * mm});
            skLineSegment(sketch, "E92.2.0.73", {"start": v(29.85, 29.57) * mm, "end": v(29.85, 25.42) * mm});
            skArc(sketch, "E92.2.0.74", {"start": v(29.12, 33.7) * mm, "mid": v(29.2, 33.9) * mm, "end": v(29.16, 34.1) * mm});
            skArc(sketch, "E92.2.0.75", {"start": v(30.1, 25.1) * mm, "mid": v(29.82, 25.26) * mm, "end": v(29.5, 25.35) * mm});
            skArc(sketch, "E92.2.0.76", {"start": v(19.98, 33.24) * mm, "mid": v(19.86, 33.18) * mm, "end": v(19.73, 33.13) * mm});
            skArc(sketch, "E92.2.0.77", {"start": v(30.02, 33.24) * mm, "mid": v(30.14, 33.18) * mm, "end": v(30.27, 33.13) * mm});
            skArc(sketch, "E92.2.0.78", {"start": v(29.85, 25.42) * mm, "mid": v(29.87, 25.34) * mm, "end": v(29.92, 25.27) * mm});
            skArc(sketch, "E92.2.0.79", {"start": v(29.16, 34.1) * mm, "mid": v(29.21, 34) * mm, "end": v(29.28, 33.9) * mm});
            skLineSegment(sketch, "E92.2.0.80", {"start": v(20.15, 29.55) * mm, "end": v(20.15, 25.42) * mm});
            skArc(sketch, "E92.2.0.81", {"start": v(20.09, 29.7) * mm, "mid": v(20, 29.78) * mm, "end": v(19.9, 29.86) * mm});
            skLineSegment(sketch, "E92.2.0.82", {"start": v(20.15, 25.35) * mm, "end": v(20.15, 25.34) * mm});
            skArc(sketch, "E92.2.0.83", {"start": v(20.5, 25.34) * mm, "mid": v(20.18, 25.26) * mm, "end": v(19.9, 25.1) * mm});
            skArc(sketch, "E92.2.0.84", {"start": v(19.9, 29.86) * mm, "mid": v(20.2, 29.72) * mm, "end": v(20.5, 29.65) * mm});
            skArc(sketch, "E92.2.0.85", {"start": v(20.15, 29.55) * mm, "mid": v(20.13, 29.63) * mm, "end": v(20.09, 29.7) * mm});
            skArc(sketch, "E92.2.0.86", {"start": v(19.9, 25.1) * mm, "mid": v(20, 25.19) * mm, "end": v(20.09, 25.27) * mm});
            skArc(sketch, "E92.2.0.87", {"start": v(29.51, 29.65) * mm, "mid": v(29.82, 29.74) * mm, "end": v(30.1, 29.89) * mm});
            skArc(sketch, "E92.2.0.88", {"start": v(30.1, 29.89) * mm, "mid": v(30, 29.8) * mm, "end": v(29.92, 29.72) * mm});
            skLineSegment(sketch, "E92.2.0.89", {"start": v(20.15, 29.65) * mm, "end": v(20.14, 29.65) * mm});
            skArc(sketch, "E92.2.0.90", {"start": v(20.09, 25.27) * mm, "mid": v(20.13, 25.34) * mm, "end": v(20.15, 25.42) * mm});
            skLineSegment(sketch, "E92.2.0.91", {"start": v(25, 32.59) * mm, "end": v(25, 22.41) * mm});
            skArc(sketch, "E92.2.0.92", {"start": v(29.92, 29.72) * mm, "mid": v(29.87, 29.65) * mm, "end": v(29.85, 29.57) * mm});
            skLineSegment(sketch, "E92.2.0.93", {"start": v(20.5, 25.34) * mm, "end": v(22.15, 25.35) * mm});
            skLineSegment(sketch, "E92.2.0.94", {"start": v(20.5, 29.65) * mm, "end": v(22.41, 29.65) * mm});
            skLineSegment(sketch, "E92.2.0.95", {"start": v(27.59, 29.65) * mm, "end": v(29.51, 29.65) * mm});
            skLineSegment(sketch, "E92.2.0.96", {"start": v(27.59, 25.35) * mm, "end": v(29.5, 25.35) * mm});
            skLineSegment(sketch, "E92.2.0.97", {"start": v(27.85, 29.65) * mm, "end": v(29.51, 29.65) * mm});
            skArc(sketch, "E92.2.0.98", {"start": v(22.85, 29.44) * mm, "mid": v(22.78, 29.75) * mm, "end": v(22.58, 30) * mm});
            skArc(sketch, "E92.2.0.99", {"start": v(22.41, 29.65) * mm, "mid": v(22.57, 29.78) * mm, "end": v(22.58, 30) * mm});
            skArc(sketch, "E92.2.0.100", {"start": v(24.6, 31.42) * mm, "mid": v(24.54, 31.64) * mm, "end": v(24.38, 31.8) * mm});
            skLineSegment(sketch, "E92.2.0.101", {"start": v(25.4, 30.3) * mm, "end": v(25.4, 31.42) * mm});
            skLineSegment(sketch, "E92.2.0.102", {"start": v(24.6, 31.42) * mm, "end": v(24.6, 30.5) * mm});
            skLineSegment(sketch, "E92.2.0.103", {"start": v(22.85, 29.44) * mm, "end": v(22.85, 25.56) * mm});
            skArc(sketch, "E92.2.0.104", {"start": v(25.62, 31.8) * mm, "mid": v(25.47, 31.64) * mm, "end": v(25.4, 31.42) * mm});
            skLineSegment(sketch, "E92.2.0.105", {"start": v(25.75, 30) * mm, "end": v(25.7, 30) * mm});
            skLineSegment(sketch, "E92.2.0.106", {"start": v(27.59, 29.65) * mm, "end": v(27.85, 29.65) * mm});
            skArc(sketch, "E92.2.0.107", {"start": v(27.15, 29.44) * mm, "mid": v(27.22, 29.75) * mm, "end": v(27.42, 30) * mm});
            skLineSegment(sketch, "E92.2.0.108", {"start": v(24.04, 30) * mm, "end": v(23.95, 30) * mm});
            skLineSegment(sketch, "E92.2.0.109", {"start": v(24.25, 30) * mm, "end": v(24.3, 30) * mm});
            skArc(sketch, "E92.2.0.110", {"start": v(22.58, 25) * mm, "mid": v(22.6, 25.23) * mm, "end": v(22.41, 25.35) * mm});
            skArc(sketch, "E92.2.0.111", {"start": v(22.58, 25) * mm, "mid": v(22.74, 25.27) * mm, "end": v(22.85, 25.56) * mm});
            skArc(sketch, "E92.2.0.112", {"start": v(24.6, 30.3) * mm, "mid": v(24.51, 30.09) * mm, "end": v(24.3, 30) * mm});
            skLineSegment(sketch, "E92.2.0.113", {"start": v(25.75, 29.79) * mm, "end": v(25.75, 28.19) * mm});
            skArc(sketch, "E92.2.0.114", {"start": v(25.96, 30) * mm, "mid": v(25.81, 29.94) * mm, "end": v(25.75, 29.79) * mm});
            skLineSegment(sketch, "E92.2.0.115", {"start": v(25.28, 27.54) * mm, "end": v(25.66, 28.04) * mm});
            skArc(sketch, "E92.2.0.116", {"start": v(24.73, 27.5) * mm, "mid": v(24.73, 27.48) * mm, "end": v(24.72, 27.46) * mm});
            skLineSegment(sketch, "E92.2.0.117", {"start": v(25.75, 30) * mm, "end": v(25.96, 30) * mm});
            skLineSegment(sketch, "E92.2.0.118", {"start": v(24.04, 30) * mm, "end": v(24.25, 30) * mm});
            skArc(sketch, "E92.2.0.119", {"start": v(27.42, 30) * mm, "mid": v(27.4, 29.77) * mm, "end": v(27.59, 29.65) * mm});
            skArc(sketch, "E92.2.0.120", {"start": v(25.4, 30.3) * mm, "mid": v(25.49, 30.09) * mm, "end": v(25.7, 30) * mm});
            skLineSegment(sketch, "E92.2.0.121", {"start": v(24.25, 25.21) * mm, "end": v(24.25, 29.79) * mm});
            skArc(sketch, "E92.2.0.122", {"start": v(24.25, 29.79) * mm, "mid": v(24.19, 29.94) * mm, "end": v(24.04, 30) * mm});
            skLineSegment(sketch, "E92.2.0.123", {"start": v(27.15, 29.44) * mm, "end": v(27.15, 25.56) * mm});
            skLineSegment(sketch, "E92.2.0.124", {"start": v(25.75, 27.5) * mm, "end": v(25.75, 26.99) * mm});
            skArc(sketch, "E92.2.0.125", {"start": v(27.42, 25) * mm, "mid": v(27.26, 25.27) * mm, "end": v(27.15, 25.56) * mm});
            skLineSegment(sketch, "E92.2.0.126", {"start": v(24.6, 24.5) * mm, "end": v(24.6, 23.58) * mm});
            skArc(sketch, "E92.2.0.127", {"start": v(24.04, 25) * mm, "mid": v(24.19, 25.06) * mm, "end": v(24.25, 25.21) * mm});
            skLineSegment(sketch, "E92.2.0.128", {"start": v(25.75, 25.21) * mm, "end": v(25.75, 26.81) * mm});
            skLineSegment(sketch, "E92.2.0.129", {"start": v(22.41, 25.35) * mm, "end": v(22.15, 25.35) * mm});
            skLineSegment(sketch, "E92.2.0.130", {"start": v(24.6, 30.5) * mm, "end": v(24.6, 30.3) * mm});
            skArc(sketch, "E92.2.0.131", {"start": v(27.59, 25.35) * mm, "mid": v(27.4, 25.23) * mm, "end": v(27.42, 25) * mm});
            skLineSegment(sketch, "E92.2.0.132", {"start": v(25.96, 30) * mm, "end": v(26.05, 30) * mm});
            skLineSegment(sketch, "E92.2.0.133", {"start": v(25.4, 24.7) * mm, "end": v(25.4, 23.58) * mm});
            skLineSegment(sketch, "E92.2.0.134", {"start": v(25.75, 28.19) * mm, "end": v(25.75, 28.01) * mm});
            skLineSegment(sketch, "E92.2.0.135", {"start": v(24.04, 25) * mm, "end": v(23.95, 25) * mm});
            skArc(sketch, "E92.2.0.136", {"start": v(24.34, 26.96) * mm, "mid": v(24.28, 26.94) * mm, "end": v(24.25, 26.99) * mm});
            skArc(sketch, "E92.2.0.137", {"start": v(24.72, 27.54) * mm, "mid": v(24.73, 27.52) * mm, "end": v(24.73, 27.5) * mm});
            skLineSegment(sketch, "E92.2.0.138", {"start": v(24.6, 24.7) * mm, "end": v(24.6, 24.5) * mm});
            skArc(sketch, "E92.2.0.139", {"start": v(25.27, 27.5) * mm, "mid": v(25.27, 27.48) * mm, "end": v(25.28, 27.46) * mm});
            skArc(sketch, "E92.2.0.140", {"start": v(25.66, 26.96) * mm, "mid": v(25.72, 26.94) * mm, "end": v(25.75, 26.99) * mm});
            skArc(sketch, "E92.2.0.141", {"start": v(23.79, 30.08) * mm, "mid": v(23.86, 30.02) * mm, "end": v(23.95, 30) * mm});
            skArc(sketch, "E92.2.0.142", {"start": v(26.21, 24.92) * mm, "mid": v(26.14, 24.98) * mm, "end": v(26.05, 25) * mm});
            skArc(sketch, "E92.2.0.143", {"start": v(24.34, 28.04) * mm, "mid": v(24.28, 28.06) * mm, "end": v(24.25, 28.01) * mm});
            skLineSegment(sketch, "E92.2.0.144", {"start": v(24.72, 27.46) * mm, "end": v(24.34, 26.96) * mm});
            skArc(sketch, "E92.2.0.145", {"start": v(25.28, 27.54) * mm, "mid": v(25.27, 27.52) * mm, "end": v(25.27, 27.5) * mm});
            skLineSegment(sketch, "E92.2.0.146", {"start": v(25.28, 27.46) * mm, "end": v(25.66, 26.96) * mm});
            skArc(sketch, "E92.2.0.147", {"start": v(27.42, 25) * mm, "mid": v(27.4, 25.23) * mm, "end": v(27.59, 25.35) * mm});
            skArc(sketch, "E92.2.0.148", {"start": v(25.4, 24.7) * mm, "mid": v(25.49, 24.91) * mm, "end": v(25.7, 25) * mm});
            skLineSegment(sketch, "E92.2.0.149", {"start": v(25.75, 26.81) * mm, "end": v(25.75, 26.99) * mm});
            skArc(sketch, "E92.2.0.150", {"start": v(24.6, 23.58) * mm, "mid": v(24.54, 23.37) * mm, "end": v(24.39, 23.2) * mm});
            skArc(sketch, "E92.2.0.151", {"start": v(26.05, 30) * mm, "mid": v(26.14, 30.02) * mm, "end": v(26.21, 30.08) * mm});
            skLineSegment(sketch, "E92.2.0.152", {"start": v(24.25, 25) * mm, "end": v(24.3, 25) * mm});
            skLineSegment(sketch, "E92.2.0.153", {"start": v(25.75, 25) * mm, "end": v(25.96, 25) * mm});
            skLineSegment(sketch, "E92.2.0.154", {"start": v(24.04, 25) * mm, "end": v(24.25, 25) * mm});
            skArc(sketch, "E92.2.0.155", {"start": v(25.75, 25.21) * mm, "mid": v(25.81, 25.06) * mm, "end": v(25.96, 25) * mm});
            skArc(sketch, "E92.2.0.156", {"start": v(25.4, 23.58) * mm, "mid": v(25.46, 23.37) * mm, "end": v(25.61, 23.2) * mm});
            skLineSegment(sketch, "E92.2.0.157", {"start": v(25.75, 27.5) * mm, "end": v(25.75, 28.01) * mm});
            skLineSegment(sketch, "E92.2.0.158", {"start": v(25.96, 25) * mm, "end": v(26.05, 25) * mm});
            skArc(sketch, "E92.2.0.159", {"start": v(24.6, 23.58) * mm, "mid": v(24.54, 23.37) * mm, "end": v(24.39, 23.2) * mm});
            skArc(sketch, "E92.2.0.160", {"start": v(25.66, 28.04) * mm, "mid": v(25.72, 28.06) * mm, "end": v(25.75, 28.01) * mm});
            skLineSegment(sketch, "E92.2.0.161", {"start": v(25.75, 25) * mm, "end": v(25.7, 25) * mm});
            skLineSegment(sketch, "E92.2.0.162", {"start": v(24.72, 27.54) * mm, "end": v(24.34, 28.04) * mm});
            skArc(sketch, "E92.2.0.163", {"start": v(24.6, 24.7) * mm, "mid": v(24.51, 24.91) * mm, "end": v(24.3, 25) * mm});
            skArc(sketch, "E92.2.0.164", {"start": v(23.95, 25) * mm, "mid": v(23.86, 24.98) * mm, "end": v(23.79, 24.92) * mm});
            skLineSegment(sketch, "E92.direction1", {"start": v(-32.94, 20.06) * mm, "end": v(-7.94, 20.06) * mm, "construction": true});
            skPoint(sketch, "E93.0.1.0", {"position": v(-32.94, 7.44) * mm});
            skPoint(sketch, "E93.0.1.1", {"position": v(-17.06, 7.44) * mm});
            skArc(sketch, "E93.0.1.2", {"start": v(-19.73, 5.63) * mm, "mid": v(-17.75, 9.02) * mm, "end": v(-20.84, 6.6) * mm});
            skPoint(sketch, "E93.0.1.4", {"position": v(-17.06, -7.44) * mm});
            skCircle(sketch, "E93.0.1.5", {"center": v(-19.06, -7.52) * mm, "radius": 2 * mm});
            skPoint(sketch, "E93.0.1.6", {"position": v(-24.49, -5.95) * mm});
            skPoint(sketch, "E93.0.1.7", {"position": v(-25, 6.09) * mm});
            skPoint(sketch, "E93.0.1.8", {"position": v(-32.94, -7.44) * mm});
            skPoint(sketch, "E93.0.1.9", {"position": v(-35.15, -0.7) * mm});
            skPoint(sketch, "E93.0.1.10", {"position": v(-23.85, 2.5) * mm});
            skPoint(sketch, "E93.0.1.11", {"position": v(-24.25, -2.5) * mm});
            skArc(sketch, "E93.0.1.12", {"start": v(-30.27, 5.63) * mm, "mid": v(-32.26, 9.01) * mm, "end": v(-29.15, 6.62) * mm});
            skPoint(sketch, "E93.0.1.13", {"position": v(-22.85, 2.15) * mm});
            skPoint(sketch, "E93.0.1.14", {"position": v(-23.85, -2.5) * mm});
            skPoint(sketch, "E93.0.1.15", {"position": v(-26.15, 2.5) * mm});
            skCircle(sketch, "E93.0.1.17", {"center": v(-30.94, -7.52) * mm, "radius": 2 * mm});
            skPoint(sketch, "E93.0.1.18", {"position": v(-27.15, 2.15) * mm});
            skPoint(sketch, "E93.0.1.19", {"position": v(-25.75, -2.5) * mm});
            skPoint(sketch, "E93.0.1.20", {"position": v(-25, -6.09) * mm});
            skPoint(sketch, "E93.0.1.21", {"position": v(-22.85, -2.15) * mm});
            skPoint(sketch, "E93.0.1.22", {"position": v(-27.15, -2.15) * mm});
            skPoint(sketch, "E93.0.1.24", {"position": v(-26.15, -2.5) * mm});
            skPoint(sketch, "E93.0.1.26", {"position": v(-22.85, 2.15) * mm});
            skPoint(sketch, "E93.0.1.27", {"position": v(-22.85, -2.15) * mm});
            skPoint(sketch, "E93.0.1.28", {"position": v(-27.15, 2.15) * mm});
            skPoint(sketch, "E93.0.1.29", {"position": v(-24.25, 2.5) * mm});
            skPoint(sketch, "E93.0.1.30", {"position": v(-25.75, 2.5) * mm});
            skPoint(sketch, "E93.0.1.31", {"position": v(-27.15, -2.15) * mm});
            skPoint(sketch, "E93.0.1.32", {"position": v(-25.75, -2.5) * mm});
            skPoint(sketch, "E93.0.1.33", {"position": v(-27.15, 2.15) * mm});
            skPoint(sketch, "E93.0.1.34", {"position": v(-25.75, 2.5) * mm});
            skPoint(sketch, "E93.0.1.35", {"position": v(-27.15, -2.15) * mm});
            skPoint(sketch, "E93.0.1.36", {"position": v(-22.85, -2.15) * mm});
            skPoint(sketch, "E93.0.1.37", {"position": v(-22.85, 2.15) * mm});
            skPoint(sketch, "E93.0.1.38", {"position": v(-25, 0) * mm});
            skPoint(sketch, "E93.0.1.39", {"position": v(-24.75, 0) * mm});
            skPoint(sketch, "E93.0.1.40", {"position": v(-24.25, -2.29) * mm});
            skPoint(sketch, "E93.0.1.41", {"position": v(-27.15, -2.15) * mm});
            skArc(sketch, "E93.0.1.42", {"start": v(-20.13, -5.54) * mm, "mid": v(-19.95, -5.64) * mm, "end": v(-19.75, -5.64) * mm});
            skLineSegment(sketch, "E93.0.1.43", {"start": v(-22.58, -2.5) * mm, "end": v(-20.13, -5.54) * mm});
            skPoint(sketch, "E93.0.1.44", {"position": v(-22.85, 2.15) * mm});
            skPoint(sketch, "E93.0.1.45", {"position": v(-22.85, -2.15) * mm});
            skLineSegment(sketch, "E93.0.1.46", {"start": v(-23.79, -2.58) * mm, "end": v(-20.88, -6.2) * mm});
            skPoint(sketch, "E93.0.1.47", {"position": v(-24.25, 0) * mm});
            skArc(sketch, "E93.0.1.48", {"start": v(-20.85, -6.62) * mm, "mid": v(-20.81, -6.4) * mm, "end": v(-20.88, -6.2) * mm});
            skArc(sketch, "E93.0.1.49", {"start": v(-24.38, 4.3) * mm, "mid": v(-25, 6.09) * mm, "end": v(-25.62, 4.3) * mm});
            skPoint(sketch, "E93.0.1.50", {"position": v(-27.15, 2.15) * mm});
            skPoint(sketch, "E93.0.1.51", {"position": v(-22.85, 2.15) * mm});
            skPoint(sketch, "E93.0.1.52", {"position": v(-27.15, 2.15) * mm});
            skPoint(sketch, "E93.0.1.53", {"position": v(-27.15, -2.15) * mm});
            skPoint(sketch, "E93.0.1.54", {"position": v(-22.85, -2.15) * mm});
            skPoint(sketch, "E93.0.1.55", {"position": v(-27.15, -2.15) * mm});
            skPoint(sketch, "E93.0.1.56", {"position": v(-22.85, -2.15) * mm});
            skArc(sketch, "E93.0.1.57", {"start": v(-29.15, -6.62) * mm, "mid": v(-29.19, -6.4) * mm, "end": v(-29.12, -6.2) * mm});
            skPoint(sketch, "E93.0.1.58", {"position": v(-27.15, 2.15) * mm});
            skArc(sketch, "E93.0.1.59", {"start": v(-29.15, 6.62) * mm, "mid": v(-29.52, 6.1) * mm, "end": v(-30.02, 5.74) * mm});
            skLineSegment(sketch, "E93.0.1.60", {"start": v(-26.21, 2.58) * mm, "end": v(-29.1, 6.19) * mm});
            skLineSegment(sketch, "E93.0.1.61", {"start": v(-27.42, -2.5) * mm, "end": v(-29.87, -5.54) * mm});
            skArc(sketch, "E93.0.1.62", {"start": v(-29.15, 6.62) * mm, "mid": v(-29.19, 6.4) * mm, "end": v(-29.1, 6.19) * mm});
            skArc(sketch, "E93.0.1.63", {"start": v(-29.87, -5.54) * mm, "mid": v(-30.05, -5.64) * mm, "end": v(-30.25, -5.64) * mm});
            skLineSegment(sketch, "E93.0.1.64", {"start": v(-27.42, 2.5) * mm, "end": v(-29.86, 5.54) * mm});
            skLineSegment(sketch, "E93.0.1.65", {"start": v(-26.21, -2.58) * mm, "end": v(-29.12, -6.2) * mm});
            skLineSegment(sketch, "E93.0.1.67", {"start": v(-22.58, 2.5) * mm, "end": v(-20.14, 5.54) * mm});
            skLineSegment(sketch, "E93.0.1.68", {"start": v(-23.79, 2.58) * mm, "end": v(-20.88, 6.2) * mm});
            skArc(sketch, "E93.0.1.69", {"start": v(-20.84, 6.6) * mm, "mid": v(-20.79, 6.5) * mm, "end": v(-20.72, 6.4) * mm});
            skLineSegment(sketch, "E93.0.1.70", {"start": v(-25, 5.09) * mm, "end": v(-25, -5.09) * mm});
            skPoint(sketch, "E93.0.1.71", {"position": v(-27.15, -2.15) * mm});
            skArc(sketch, "E93.0.1.72", {"start": v(-20.72, 6.4) * mm, "mid": v(-20.4, 6.02) * mm, "end": v(-19.98, 5.74) * mm});
            skPoint(sketch, "E93.0.1.73", {"position": v(-22.85, -2.15) * mm});
            skArc(sketch, "E93.0.1.74", {"start": v(-29.86, 5.54) * mm, "mid": v(-30.05, 5.63) * mm, "end": v(-30.27, 5.63) * mm});
            skArc(sketch, "E93.0.1.75", {"start": v(-19.73, 5.63) * mm, "mid": v(-19.94, 5.63) * mm, "end": v(-20.14, 5.54) * mm});
            skArc(sketch, "E93.0.1.76", {"start": v(-19.98, 5.74) * mm, "mid": v(-19.86, 5.68) * mm, "end": v(-19.73, 5.63) * mm});
            skArc(sketch, "E93.0.1.77", {"start": v(-30.02, 5.74) * mm, "mid": v(-30.14, 5.68) * mm, "end": v(-30.27, 5.63) * mm});
            skArc(sketch, "E93.0.1.78", {"start": v(-20.88, 6.2) * mm, "mid": v(-20.8, 6.4) * mm, "end": v(-20.84, 6.6) * mm});
            skArc(sketch, "E93.0.1.79", {"start": v(-25.61, -4.3) * mm, "mid": v(-25, -6.09) * mm, "end": v(-24.39, -4.3) * mm});
            skArc(sketch, "E93.0.1.87", {"start": v(-29.91, 2.2) * mm, "mid": v(-30, 2.28) * mm, "end": v(-30.1, 2.36) * mm});
            skArc(sketch, "E93.0.1.94", {"start": v(-29.85, 2.05) * mm, "mid": v(-29.87, 2.13) * mm, "end": v(-29.91, 2.2) * mm});
            skLineSegment(sketch, "E93.0.1.97", {"start": v(-29.85, 2.15) * mm, "end": v(-29.86, 2.15) * mm});
            skArc(sketch, "E93.0.1.98", {"start": v(-30.1, 2.36) * mm, "mid": v(-29.8, 2.22) * mm, "end": v(-29.5, 2.15) * mm});
            skLineSegment(sketch, "E93.0.1.99", {"start": v(-27.15, 1.94) * mm, "end": v(-27.15, -1.94) * mm});
            skArc(sketch, "E93.0.1.100", {"start": v(-24.6, -3.92) * mm, "mid": v(-24.54, -4.13) * mm, "end": v(-24.39, -4.3) * mm});
            skArc(sketch, "E93.0.1.102", {"start": v(-25.4, -3.92) * mm, "mid": v(-25.46, -4.13) * mm, "end": v(-25.61, -4.3) * mm});
            skLineSegment(sketch, "E93.0.1.103", {"start": v(-25.4, -3) * mm, "end": v(-25.4, -3.92) * mm});
            skLineSegment(sketch, "E93.0.1.104", {"start": v(-24.6, -2.8) * mm, "end": v(-24.6, -3.92) * mm});
            skArc(sketch, "E93.0.1.106", {"start": v(-27.42, -2.5) * mm, "mid": v(-27.26, -2.23) * mm, "end": v(-27.15, -1.94) * mm});
            skLineSegment(sketch, "E93.0.1.107", {"start": v(-25.96, -2.5) * mm, "end": v(-25.75, -2.5) * mm});
            skLineSegment(sketch, "E93.0.1.108", {"start": v(-25.4, 3) * mm, "end": v(-25.4, 2.8) * mm});
            skArc(sketch, "E93.0.1.109", {"start": v(-24.6, -2.8) * mm, "mid": v(-24.51, -2.59) * mm, "end": v(-24.3, -2.5) * mm});
            skArc(sketch, "E93.0.1.110", {"start": v(-25.4, -3.92) * mm, "mid": v(-25.46, -4.13) * mm, "end": v(-25.61, -4.3) * mm});
            skArc(sketch, "E93.0.1.111", {"start": v(-27.15, 1.94) * mm, "mid": v(-27.22, 2.25) * mm, "end": v(-27.42, 2.5) * mm});
            skArc(sketch, "E93.0.1.112", {"start": v(-24.38, 4.3) * mm, "mid": v(-24.53, 4.14) * mm, "end": v(-24.6, 3.92) * mm});
            skArc(sketch, "E93.0.1.113", {"start": v(-24.6, 2.8) * mm, "mid": v(-24.51, 2.59) * mm, "end": v(-24.3, 2.5) * mm});
            skLineSegment(sketch, "E93.0.1.115", {"start": v(-24.25, -2.29) * mm, "end": v(-24.25, -0.69) * mm});
            skArc(sketch, "E93.0.1.116", {"start": v(-25.4, 3.92) * mm, "mid": v(-25.46, 4.14) * mm, "end": v(-25.62, 4.3) * mm});
            skArc(sketch, "E93.0.1.117", {"start": v(-25.4, -2.8) * mm, "mid": v(-25.49, -2.59) * mm, "end": v(-25.7, -2.5) * mm});
            skLineSegment(sketch, "E93.0.1.119", {"start": v(-25.4, -2.8) * mm, "end": v(-25.4, -3) * mm});
            skLineSegment(sketch, "E93.0.1.120", {"start": v(-24.6, 2.8) * mm, "end": v(-24.6, 3.92) * mm});
            skLineSegment(sketch, "E93.0.1.121", {"start": v(-24.04, -2.5) * mm, "end": v(-23.95, -2.5) * mm});
            skArc(sketch, "E93.0.1.122", {"start": v(-25.96, -2.5) * mm, "mid": v(-25.81, -2.44) * mm, "end": v(-25.75, -2.29) * mm});
            skLineSegment(sketch, "E93.0.1.123", {"start": v(-25.4, 3.92) * mm, "end": v(-25.4, 3) * mm});
            skArc(sketch, "E93.0.1.124", {"start": v(-22.58, -2.5) * mm, "mid": v(-22.74, -2.23) * mm, "end": v(-22.85, -1.94) * mm});
            skLineSegment(sketch, "E93.0.1.125", {"start": v(-24.04, 2.5) * mm, "end": v(-23.95, 2.5) * mm});
            skLineSegment(sketch, "E93.0.1.126", {"start": v(-22.85, 1.94) * mm, "end": v(-22.85, -1.94) * mm});
            skLineSegment(sketch, "E93.0.1.127", {"start": v(-24.25, -2.5) * mm, "end": v(-24.04, -2.5) * mm});
            skLineSegment(sketch, "E93.0.1.128", {"start": v(-24.72, -0.04) * mm, "end": v(-24.34, -0.54) * mm});
            skArc(sketch, "E93.0.1.129", {"start": v(-23.79, -2.58) * mm, "mid": v(-23.86, -2.52) * mm, "end": v(-23.95, -2.5) * mm});
            skLineSegment(sketch, "E93.0.1.130", {"start": v(-24.72, 0.04) * mm, "end": v(-24.34, 0.54) * mm});
            skLineSegment(sketch, "E93.0.1.131", {"start": v(-24.25, 2.29) * mm, "end": v(-24.25, 0.69) * mm});
            skLineSegment(sketch, "E93.0.1.132", {"start": v(-25.28, -0.04) * mm, "end": v(-25.66, -0.54) * mm});
            skLineSegment(sketch, "E93.0.1.133", {"start": v(-25.75, -2.29) * mm, "end": v(-25.75, 2.29) * mm});
            skArc(sketch, "E93.0.1.135", {"start": v(-25.4, 2.8) * mm, "mid": v(-25.49, 2.59) * mm, "end": v(-25.7, 2.5) * mm});
            skLineSegment(sketch, "E93.0.1.136", {"start": v(-24.25, 0) * mm, "end": v(-24.25, 0.51) * mm});
            skArc(sketch, "E93.0.1.137", {"start": v(-22.85, 1.94) * mm, "mid": v(-22.78, 2.25) * mm, "end": v(-22.58, 2.5) * mm});
            skLineSegment(sketch, "E93.0.1.138", {"start": v(-25.96, 2.5) * mm, "end": v(-25.75, 2.5) * mm});
            skArc(sketch, "E93.0.1.139", {"start": v(-25.66, 0.54) * mm, "mid": v(-25.72, 0.56) * mm, "end": v(-25.75, 0.51) * mm});
            skArc(sketch, "E93.0.1.140", {"start": v(-24.25, -2.29) * mm, "mid": v(-24.19, -2.44) * mm, "end": v(-24.04, -2.5) * mm});
            skLineSegment(sketch, "E93.0.1.141", {"start": v(-24.25, -0.69) * mm, "end": v(-24.25, -0.51) * mm});
            skArc(sketch, "E93.0.1.142", {"start": v(-26.05, -2.5) * mm, "mid": v(-26.14, -2.52) * mm, "end": v(-26.21, -2.58) * mm});
            skArc(sketch, "E93.0.1.143", {"start": v(-25.66, -0.54) * mm, "mid": v(-25.72, -0.56) * mm, "end": v(-25.75, -0.51) * mm});
            skLineSegment(sketch, "E93.0.1.144", {"start": v(-24.25, 2.5) * mm, "end": v(-24.04, 2.5) * mm});
            skLineSegment(sketch, "E93.0.1.145", {"start": v(-25.75, -2.5) * mm, "end": v(-25.7, -2.5) * mm});
            skLineSegment(sketch, "E93.0.1.146", {"start": v(-25.28, 0.04) * mm, "end": v(-25.66, 0.54) * mm});
            skLineSegment(sketch, "E93.0.1.147", {"start": v(-24.25, 0.69) * mm, "end": v(-24.25, 0.51) * mm});
            skArc(sketch, "E93.0.1.148", {"start": v(-24.04, 2.5) * mm, "mid": v(-24.19, 2.44) * mm, "end": v(-24.25, 2.29) * mm});
            skLineSegment(sketch, "E93.0.1.149", {"start": v(-25.96, -2.5) * mm, "end": v(-26.05, -2.5) * mm});
            skLineSegment(sketch, "E93.0.1.151", {"start": v(-24.25, -2.5) * mm, "end": v(-24.3, -2.5) * mm});
            skArc(sketch, "E93.0.1.152", {"start": v(-24.73, 0) * mm, "mid": v(-24.73, -0.02) * mm, "end": v(-24.72, -0.04) * mm});
            skArc(sketch, "E93.0.1.153", {"start": v(-25.75, 2.29) * mm, "mid": v(-25.81, 2.44) * mm, "end": v(-25.96, 2.5) * mm});
            skArc(sketch, "E93.0.1.154", {"start": v(-25.27, 0) * mm, "mid": v(-25.27, -0.02) * mm, "end": v(-25.28, -0.04) * mm});
            skLineSegment(sketch, "E93.0.1.155", {"start": v(-24.25, 0) * mm, "end": v(-24.25, -0.51) * mm});
            skArc(sketch, "E93.0.1.156", {"start": v(-26.21, 2.58) * mm, "mid": v(-26.14, 2.52) * mm, "end": v(-26.05, 2.5) * mm});
            skArc(sketch, "E93.0.1.157", {"start": v(-24.72, 0.04) * mm, "mid": v(-24.73, 0.02) * mm, "end": v(-24.73, 0) * mm});
            skArc(sketch, "E93.0.1.158", {"start": v(-24.34, 0.54) * mm, "mid": v(-24.28, 0.56) * mm, "end": v(-24.25, 0.51) * mm});
            skArc(sketch, "E93.0.1.159", {"start": v(-24.34, -0.54) * mm, "mid": v(-24.28, -0.56) * mm, "end": v(-24.25, -0.51) * mm});
            skArc(sketch, "E93.0.1.160", {"start": v(-23.95, 2.5) * mm, "mid": v(-23.86, 2.52) * mm, "end": v(-23.79, 2.58) * mm});
            skArc(sketch, "E93.0.1.161", {"start": v(-25.28, 0.04) * mm, "mid": v(-25.27, 0.02) * mm, "end": v(-25.27, 0) * mm});
            skLineSegment(sketch, "E93.0.1.163", {"start": v(-25.75, 2.5) * mm, "end": v(-25.7, 2.5) * mm});
            skLineSegment(sketch, "E93.0.1.164", {"start": v(-25.96, 2.5) * mm, "end": v(-26.05, 2.5) * mm});
            skLineSegment(sketch, "E93.0.1.165", {"start": v(-24.25, 2.5) * mm, "end": v(-24.3, 2.5) * mm});
            skLineSegment(sketch, "E93.direction2", {"start": v(-32.94, 20.06) * mm, "end": v(-32.94, -7.44) * mm, "construction": true});
            skArc(sketch, "E94.1.0.0", {"start": v(0.62, 4.3) * mm, "mid": v(0, 6.09) * mm, "end": v(-0.62, 4.3) * mm});
            skArc(sketch, "E94.1.0.1", {"start": v(-0.61, -4.3) * mm, "mid": v(0, -6.09) * mm, "end": v(0.61, -4.3) * mm});
            skPoint(sketch, "E94.1.0.2", {"position": v(-1.15, -2.5) * mm});
            skPoint(sketch, "E94.1.0.3", {"position": v(2.15, -2.15) * mm});
            skLineSegment(sketch, "E94.1.0.4", {"start": v(-2.42, 2.5) * mm, "end": v(-4.86, 5.54) * mm});
            skPoint(sketch, "E94.1.0.5", {"position": v(0.51, -5.95) * mm});
            skArc(sketch, "E94.1.0.6", {"start": v(-5.27, 5.63) * mm, "mid": v(-7.26, 9.01) * mm, "end": v(-4.15, 6.62) * mm});
            skPoint(sketch, "E94.1.0.7", {"position": v(7.94, 7.44) * mm});
            skPoint(sketch, "E94.1.0.8", {"position": v(-7.94, -7.44) * mm});
            skPoint(sketch, "E94.1.0.9", {"position": v(7.94, -7.44) * mm});
            skLineSegment(sketch, "E94.1.0.10", {"start": v(2.15, 1.94) * mm, "end": v(2.15, -1.94) * mm});
            skPoint(sketch, "E94.1.0.11", {"position": v(-0.75, -2.5) * mm});
            skPoint(sketch, "E94.1.0.12", {"position": v(0.75, 0) * mm});
            skPoint(sketch, "E94.1.0.13", {"position": v(1.15, 2.5) * mm});
            skPoint(sketch, "E94.1.0.14", {"position": v(0, 6.09) * mm});
            skLineSegment(sketch, "E94.1.0.15", {"start": v(1.21, 2.58) * mm, "end": v(4.12, 6.2) * mm});
            skLineSegment(sketch, "E94.1.0.16", {"start": v(2.42, 2.5) * mm, "end": v(4.86, 5.54) * mm});
            skPoint(sketch, "E94.1.0.17", {"position": v(-7.94, 7.44) * mm});
            skPoint(sketch, "E94.1.0.18", {"position": v(-2.15, -2.15) * mm});
            skPoint(sketch, "E94.1.0.19", {"position": v(0, -6.09) * mm});
            skPoint(sketch, "E94.1.0.20", {"position": v(0.75, -2.29) * mm});
            skLineSegment(sketch, "E94.1.0.21", {"start": v(-1.21, 2.58) * mm, "end": v(-4.1, 6.19) * mm});
            skPoint(sketch, "E94.1.0.22", {"position": v(0.75, -2.5) * mm});
            skPoint(sketch, "E94.1.0.23", {"position": v(-1.15, 2.5) * mm});
            skLineSegment(sketch, "E94.1.0.24", {"start": v(1.21, -2.58) * mm, "end": v(4.12, -6.2) * mm});
            skPoint(sketch, "E94.1.0.25", {"position": v(0.75, 2.5) * mm});
            skPoint(sketch, "E94.1.0.26", {"position": v(1.15, -2.5) * mm});
            skArc(sketch, "E94.1.0.27", {"start": v(5.27, 5.63) * mm, "mid": v(7.25, 9.02) * mm, "end": v(4.16, 6.6) * mm});
            skPoint(sketch, "E94.1.0.28", {"position": v(-10.15, -0.7) * mm});
            skCircle(sketch, "E94.1.0.29", {"center": v(5.94, -7.52) * mm, "radius": 2 * mm});
            skPoint(sketch, "E94.1.0.30", {"position": v(-0.75, 2.5) * mm});
            skLineSegment(sketch, "E94.1.0.31", {"start": v(0, 5.09) * mm, "end": v(0, -5.09) * mm});
            skLineSegment(sketch, "E94.1.0.32", {"start": v(0.4, -2.8) * mm, "end": v(0.4, -3.92) * mm});
            skLineSegment(sketch, "E94.1.0.33", {"start": v(-1.21, -2.58) * mm, "end": v(-4.12, -6.2) * mm});
            skLineSegment(sketch, "E94.1.0.34", {"start": v(-0.75, -2.29) * mm, "end": v(-0.75, 2.29) * mm});
            skLineSegment(sketch, "E94.1.0.35", {"start": v(-2.15, 1.94) * mm, "end": v(-2.15, -1.94) * mm});
            skLineSegment(sketch, "E94.1.0.36", {"start": v(0.75, 2.29) * mm, "end": v(0.75, 0.69) * mm});
            skLineSegment(sketch, "E94.1.0.37", {"start": v(-2.42, -2.5) * mm, "end": v(-4.87, -5.54) * mm});
            skLineSegment(sketch, "E94.1.0.38", {"start": v(0.75, -2.29) * mm, "end": v(0.75, -0.69) * mm});
            skCircle(sketch, "E94.1.0.39", {"center": v(-5.94, -7.52) * mm, "radius": 2 * mm});
            skLineSegment(sketch, "E94.1.0.40", {"start": v(0.4, 2.8) * mm, "end": v(0.4, 3.92) * mm});
            skPoint(sketch, "E94.1.0.41", {"position": v(-2.15, 2.15) * mm});
            skLineSegment(sketch, "E94.1.0.42", {"start": v(2.42, -2.5) * mm, "end": v(4.87, -5.54) * mm});
            skPoint(sketch, "E94.1.0.43", {"position": v(2.15, 2.15) * mm});
            skPoint(sketch, "E94.1.0.44", {"position": v(0, 0) * mm});
            skPoint(sketch, "E94.1.0.45", {"position": v(-0.75, 2.5) * mm});
            skPoint(sketch, "E94.1.0.46", {"position": v(-0.75, -2.5) * mm});
            skPoint(sketch, "E94.1.0.47", {"position": v(2.15, 2.15) * mm});
            skPoint(sketch, "E94.1.0.48", {"position": v(-2.15, 2.15) * mm});
            skPoint(sketch, "E94.1.0.49", {"position": v(-2.15, -2.15) * mm});
            skPoint(sketch, "E94.1.0.50", {"position": v(0.25, 0) * mm});
            skPoint(sketch, "E94.1.0.51", {"position": v(2.15, -2.15) * mm});
            skArc(sketch, "E94.1.0.52", {"start": v(4.15, -6.62) * mm, "mid": v(4.19, -6.4) * mm, "end": v(4.12, -6.2) * mm});
            skArc(sketch, "E94.1.0.53", {"start": v(-0.4, 3.92) * mm, "mid": v(-0.46, 4.14) * mm, "end": v(-0.62, 4.3) * mm});
            skPoint(sketch, "E94.1.0.54", {"position": v(-2.15, 2.15) * mm});
            skPoint(sketch, "E94.1.0.55", {"position": v(2.15, -2.15) * mm});
            skArc(sketch, "E94.1.0.56", {"start": v(4.28, 6.4) * mm, "mid": v(4.6, 6.02) * mm, "end": v(5.02, 5.74) * mm});
            skArc(sketch, "E94.1.0.57", {"start": v(-4.15, -6.62) * mm, "mid": v(-4.19, -6.4) * mm, "end": v(-4.12, -6.2) * mm});
            skArc(sketch, "E94.1.0.58", {"start": v(4.87, -5.54) * mm, "mid": v(5.05, -5.64) * mm, "end": v(5.25, -5.64) * mm});
            skArc(sketch, "E94.1.0.59", {"start": v(0.62, 4.3) * mm, "mid": v(0.47, 4.14) * mm, "end": v(0.4, 3.92) * mm});
            skArc(sketch, "E94.1.0.60", {"start": v(-4.15, 6.62) * mm, "mid": v(-4.52, 6.1) * mm, "end": v(-5.02, 5.74) * mm});
            skArc(sketch, "E94.1.0.61", {"start": v(-4.87, -5.54) * mm, "mid": v(-5.05, -5.64) * mm, "end": v(-5.25, -5.64) * mm});
            skPoint(sketch, "E94.1.0.62", {"position": v(2.15, 2.15) * mm});
            skArc(sketch, "E94.1.0.63", {"start": v(0.4, -3.92) * mm, "mid": v(0.46, -4.13) * mm, "end": v(0.61, -4.3) * mm});
            skLineSegment(sketch, "E94.1.0.64", {"start": v(-0.4, 3.92) * mm, "end": v(-0.4, 3) * mm});
            skLineSegment(sketch, "E94.1.0.65", {"start": v(-0.4, -3) * mm, "end": v(-0.4, -3.92) * mm});
            skPoint(sketch, "E94.1.0.66", {"position": v(-2.15, -2.15) * mm});
            skArc(sketch, "E94.1.0.67", {"start": v(5.02, 5.74) * mm, "mid": v(5.14, 5.68) * mm, "end": v(5.27, 5.63) * mm});
            skPoint(sketch, "E94.1.0.68", {"position": v(-2.15, -2.15) * mm});
            skPoint(sketch, "E94.1.0.69", {"position": v(2.15, 2.15) * mm});
            skLineSegment(sketch, "E94.1.0.70", {"start": v(0.75, 0) * mm, "end": v(0.75, 0.51) * mm});
            skArc(sketch, "E94.1.0.71", {"start": v(-4.15, 6.62) * mm, "mid": v(-4.19, 6.4) * mm, "end": v(-4.1, 6.19) * mm});
            skArc(sketch, "E94.1.0.72", {"start": v(-0.4, -3.92) * mm, "mid": v(-0.46, -4.13) * mm, "end": v(-0.61, -4.3) * mm});
            skArc(sketch, "E94.1.0.73", {"start": v(0.4, 2.8) * mm, "mid": v(0.49, 2.59) * mm, "end": v(0.7, 2.5) * mm});
            skArc(sketch, "E94.1.0.74", {"start": v(-0.66, -0.54) * mm, "mid": v(-0.72, -0.56) * mm, "end": v(-0.75, -0.51) * mm});
            skArc(sketch, "E94.1.0.75", {"start": v(5.27, 5.63) * mm, "mid": v(5.06, 5.63) * mm, "end": v(4.86, 5.54) * mm});
            skArc(sketch, "E94.1.0.76", {"start": v(0.4, -2.8) * mm, "mid": v(0.49, -2.59) * mm, "end": v(0.7, -2.5) * mm});
            skArc(sketch, "E94.1.0.77", {"start": v(4.12, 6.2) * mm, "mid": v(4.2, 6.4) * mm, "end": v(4.16, 6.6) * mm});
            skArc(sketch, "E94.1.0.78", {"start": v(-4.86, 5.54) * mm, "mid": v(-5.05, 5.63) * mm, "end": v(-5.27, 5.63) * mm});
            skPoint(sketch, "E94.1.0.79", {"position": v(-2.15, 2.15) * mm});
            skArc(sketch, "E94.1.0.80", {"start": v(-0.66, 0.54) * mm, "mid": v(-0.72, 0.56) * mm, "end": v(-0.75, 0.51) * mm});
            skArc(sketch, "E94.1.0.81", {"start": v(4.16, 6.6) * mm, "mid": v(4.21, 6.5) * mm, "end": v(4.28, 6.4) * mm});
            skArc(sketch, "E94.1.0.82", {"start": v(-5.02, 5.74) * mm, "mid": v(-5.14, 5.68) * mm, "end": v(-5.27, 5.63) * mm});
            skPoint(sketch, "E94.1.0.83", {"position": v(2.15, -2.15) * mm});
            skLineSegment(sketch, "E94.1.0.84", {"start": v(0.28, 0.04) * mm, "end": v(0.66, 0.54) * mm});
            skLineSegment(sketch, "E94.1.0.85", {"start": v(0.75, 0.69) * mm, "end": v(0.75, 0.51) * mm});
            skArc(sketch, "E94.1.0.86", {"start": v(-0.4, 2.8) * mm, "mid": v(-0.49, 2.59) * mm, "end": v(-0.7, 2.5) * mm});
            skPoint(sketch, "E94.1.0.87", {"position": v(-2.15, -2.15) * mm});
            skPoint(sketch, "E94.1.0.88", {"position": v(-2.15, 2.15) * mm});
            skLineSegment(sketch, "E94.1.0.89", {"start": v(-0.4, 3) * mm, "end": v(-0.4, 2.8) * mm});
            skLineSegment(sketch, "E94.1.0.90", {"start": v(-0.4, -2.8) * mm, "end": v(-0.4, -3) * mm});
            skLineSegment(sketch, "E94.1.0.91", {"start": v(0.75, -0.69) * mm, "end": v(0.75, -0.51) * mm});
            skLineSegment(sketch, "E94.1.0.92", {"start": v(0.75, 0) * mm, "end": v(0.75, -0.51) * mm});
            skPoint(sketch, "E94.1.0.93", {"position": v(2.15, -2.15) * mm});
            skLineSegment(sketch, "E94.1.0.94", {"start": v(-0.28, 0.04) * mm, "end": v(-0.66, 0.54) * mm});
            skArc(sketch, "E94.1.0.95", {"start": v(0.66, -0.54) * mm, "mid": v(0.72, -0.56) * mm, "end": v(0.75, -0.51) * mm});
            skArc(sketch, "E94.1.0.96", {"start": v(-5.1, 2.36) * mm, "mid": v(-4.8, 2.22) * mm, "end": v(-4.5, 2.15) * mm});
            skLineSegment(sketch, "E94.1.0.97", {"start": v(-4.85, 2.15) * mm, "end": v(-4.86, 2.15) * mm});
            skPoint(sketch, "E94.1.0.98", {"position": v(2.15, 2.15) * mm});
            skArc(sketch, "E94.1.0.99", {"start": v(-0.4, -3.92) * mm, "mid": v(-0.46, -4.13) * mm, "end": v(-0.61, -4.3) * mm});
            skArc(sketch, "E94.1.0.100", {"start": v(-0.4, -2.8) * mm, "mid": v(-0.49, -2.59) * mm, "end": v(-0.7, -2.5) * mm});
            skPoint(sketch, "E94.1.0.101", {"position": v(-2.15, -2.15) * mm});
            skPoint(sketch, "E94.1.0.102", {"position": v(-2.15, 2.15) * mm});
            skArc(sketch, "E94.1.0.103", {"start": v(-4.91, 2.2) * mm, "mid": v(-5, 2.28) * mm, "end": v(-5.1, 2.36) * mm});
            skArc(sketch, "E94.1.0.104", {"start": v(-1.05, -2.5) * mm, "mid": v(-1.14, -2.52) * mm, "end": v(-1.21, -2.58) * mm});
            skPoint(sketch, "E94.1.0.105", {"position": v(2.15, -2.15) * mm});
            skArc(sketch, "E94.1.0.106", {"start": v(0.66, 0.54) * mm, "mid": v(0.72, 0.56) * mm, "end": v(0.75, 0.51) * mm});
            skLineSegment(sketch, "E94.1.0.107", {"start": v(-0.96, -2.5) * mm, "end": v(-1.05, -2.5) * mm});
            skArc(sketch, "E94.1.0.108", {"start": v(2.15, 1.94) * mm, "mid": v(2.22, 2.25) * mm, "end": v(2.42, 2.5) * mm});
            skArc(sketch, "E94.1.0.109", {"start": v(-4.85, 2.05) * mm, "mid": v(-4.87, 2.13) * mm, "end": v(-4.91, 2.2) * mm});
            skArc(sketch, "E94.1.0.110", {"start": v(-0.96, -2.5) * mm, "mid": v(-0.81, -2.44) * mm, "end": v(-0.75, -2.29) * mm});
            skArc(sketch, "E94.1.0.111", {"start": v(1.21, -2.58) * mm, "mid": v(1.14, -2.52) * mm, "end": v(1.05, -2.5) * mm});
            skLineSegment(sketch, "E94.1.0.112", {"start": v(0.96, -2.5) * mm, "end": v(1.05, -2.5) * mm});
            skLineSegment(sketch, "E94.1.0.113", {"start": v(-0.96, 2.5) * mm, "end": v(-0.75, 2.5) * mm});
            skLineSegment(sketch, "E94.1.0.114", {"start": v(-0.96, 2.5) * mm, "end": v(-1.05, 2.5) * mm});
            skLineSegment(sketch, "E94.1.0.115", {"start": v(-0.75, 2.5) * mm, "end": v(-0.7, 2.5) * mm});
            skArc(sketch, "E94.1.0.116", {"start": v(1.05, 2.5) * mm, "mid": v(1.14, 2.52) * mm, "end": v(1.21, 2.58) * mm});
            skLineSegment(sketch, "E94.1.0.117", {"start": v(-0.96, -2.5) * mm, "end": v(-0.75, -2.5) * mm});
            skLineSegment(sketch, "E94.1.0.118", {"start": v(0.75, 2.5) * mm, "end": v(0.7, 2.5) * mm});
            skPoint(sketch, "E94.1.0.119", {"position": v(-2.15, -2.15) * mm});
            skLineSegment(sketch, "E94.1.0.120", {"start": v(0.75, -2.5) * mm, "end": v(0.7, -2.5) * mm});
            skArc(sketch, "E94.1.0.121", {"start": v(-0.75, 2.29) * mm, "mid": v(-0.81, 2.44) * mm, "end": v(-0.96, 2.5) * mm});
            skPoint(sketch, "E94.1.0.122", {"position": v(2.15, -2.15) * mm});
            skLineSegment(sketch, "E94.1.0.123", {"start": v(-0.28, -0.04) * mm, "end": v(-0.66, -0.54) * mm});
            skArc(sketch, "E94.1.0.124", {"start": v(0.96, 2.5) * mm, "mid": v(0.81, 2.44) * mm, "end": v(0.75, 2.29) * mm});
            skArc(sketch, "E94.1.0.125", {"start": v(-0.27, 0) * mm, "mid": v(-0.27, -0.02) * mm, "end": v(-0.28, -0.04) * mm});
            skArc(sketch, "E94.1.0.126", {"start": v(0.75, -2.29) * mm, "mid": v(0.81, -2.44) * mm, "end": v(0.96, -2.5) * mm});
            skArc(sketch, "E94.1.0.127", {"start": v(-1.21, 2.58) * mm, "mid": v(-1.14, 2.52) * mm, "end": v(-1.05, 2.5) * mm});
            skLineSegment(sketch, "E94.1.0.128", {"start": v(-0.75, -2.5) * mm, "end": v(-0.7, -2.5) * mm});
            skArc(sketch, "E94.1.0.129", {"start": v(-2.15, 1.94) * mm, "mid": v(-2.22, 2.25) * mm, "end": v(-2.42, 2.5) * mm});
            skLineSegment(sketch, "E94.1.0.130", {"start": v(0.75, 2.5) * mm, "end": v(0.96, 2.5) * mm});
            skLineSegment(sketch, "E94.1.0.131", {"start": v(0.75, -2.5) * mm, "end": v(0.96, -2.5) * mm});
            skArc(sketch, "E94.1.0.132", {"start": v(-0.28, 0.04) * mm, "mid": v(-0.27, 0.02) * mm, "end": v(-0.27, 0) * mm});
            skArc(sketch, "E94.1.0.133", {"start": v(-2.42, -2.5) * mm, "mid": v(-2.26, -2.23) * mm, "end": v(-2.15, -1.94) * mm});
            skLineSegment(sketch, "E94.1.0.134", {"start": v(0.96, 2.5) * mm, "end": v(1.05, 2.5) * mm});
            skArc(sketch, "E94.1.0.135", {"start": v(2.42, -2.5) * mm, "mid": v(2.26, -2.23) * mm, "end": v(2.15, -1.94) * mm});
            skArc(sketch, "E94.1.0.136", {"start": v(0.27, 0) * mm, "mid": v(0.27, -0.02) * mm, "end": v(0.28, -0.04) * mm});
            skLineSegment(sketch, "E94.1.0.137", {"start": v(0.28, -0.04) * mm, "end": v(0.66, -0.54) * mm});
            skArc(sketch, "E94.1.0.138", {"start": v(0.28, 0.04) * mm, "mid": v(0.27, 0.02) * mm, "end": v(0.27, 0) * mm});
            skArc(sketch, "E94.2.0.0", {"start": v(25.62, 4.3) * mm, "mid": v(25, 6.09) * mm, "end": v(24.38, 4.3) * mm});
            skArc(sketch, "E94.2.0.1", {"start": v(24.39, -4.3) * mm, "mid": v(25, -6.09) * mm, "end": v(25.61, -4.3) * mm});
            skPoint(sketch, "E94.2.0.2", {"position": v(23.85, -2.5) * mm});
            skPoint(sketch, "E94.2.0.3", {"position": v(27.15, -2.15) * mm});
            skLineSegment(sketch, "E94.2.0.4", {"start": v(22.58, 2.5) * mm, "end": v(20.14, 5.54) * mm});
            skPoint(sketch, "E94.2.0.5", {"position": v(25.51, -5.95) * mm});
            skArc(sketch, "E94.2.0.6", {"start": v(19.73, 5.63) * mm, "mid": v(17.74, 9.01) * mm, "end": v(20.85, 6.62) * mm});
            skPoint(sketch, "E94.2.0.7", {"position": v(32.94, 7.44) * mm});
            skPoint(sketch, "E94.2.0.8", {"position": v(17.06, -7.44) * mm});
            skPoint(sketch, "E94.2.0.9", {"position": v(32.94, -7.44) * mm});
            skLineSegment(sketch, "E94.2.0.10", {"start": v(27.15, 1.94) * mm, "end": v(27.15, -1.94) * mm});
            skPoint(sketch, "E94.2.0.11", {"position": v(24.25, -2.5) * mm});
            skPoint(sketch, "E94.2.0.12", {"position": v(25.75, 0) * mm});
            skPoint(sketch, "E94.2.0.13", {"position": v(26.15, 2.5) * mm});
            skPoint(sketch, "E94.2.0.14", {"position": v(25, 6.09) * mm});
            skLineSegment(sketch, "E94.2.0.15", {"start": v(26.21, 2.58) * mm, "end": v(29.12, 6.2) * mm});
            skLineSegment(sketch, "E94.2.0.16", {"start": v(27.42, 2.5) * mm, "end": v(29.86, 5.54) * mm});
            skPoint(sketch, "E94.2.0.17", {"position": v(17.06, 7.44) * mm});
            skPoint(sketch, "E94.2.0.18", {"position": v(22.85, -2.15) * mm});
            skPoint(sketch, "E94.2.0.19", {"position": v(25, -6.09) * mm});
            skPoint(sketch, "E94.2.0.20", {"position": v(25.75, -2.29) * mm});
            skLineSegment(sketch, "E94.2.0.21", {"start": v(23.79, 2.58) * mm, "end": v(20.9, 6.19) * mm});
            skPoint(sketch, "E94.2.0.22", {"position": v(25.75, -2.5) * mm});
            skPoint(sketch, "E94.2.0.23", {"position": v(23.85, 2.5) * mm});
            skLineSegment(sketch, "E94.2.0.24", {"start": v(26.21, -2.58) * mm, "end": v(29.12, -6.2) * mm});
            skPoint(sketch, "E94.2.0.25", {"position": v(25.75, 2.5) * mm});
            skPoint(sketch, "E94.2.0.26", {"position": v(26.15, -2.5) * mm});
            skArc(sketch, "E94.2.0.27", {"start": v(30.27, 5.63) * mm, "mid": v(32.25, 9.02) * mm, "end": v(29.16, 6.6) * mm});
            skPoint(sketch, "E94.2.0.28", {"position": v(14.85, -0.7) * mm});
            skCircle(sketch, "E94.2.0.29", {"center": v(30.94, -7.52) * mm, "radius": 2 * mm});
            skPoint(sketch, "E94.2.0.30", {"position": v(24.25, 2.5) * mm});
            skLineSegment(sketch, "E94.2.0.31", {"start": v(25, 5.09) * mm, "end": v(25, -5.09) * mm});
            skLineSegment(sketch, "E94.2.0.32", {"start": v(25.4, -2.8) * mm, "end": v(25.4, -3.92) * mm});
            skLineSegment(sketch, "E94.2.0.33", {"start": v(23.79, -2.58) * mm, "end": v(20.88, -6.2) * mm});
            skLineSegment(sketch, "E94.2.0.34", {"start": v(24.25, -2.29) * mm, "end": v(24.25, 2.29) * mm});
            skLineSegment(sketch, "E94.2.0.35", {"start": v(22.85, 1.94) * mm, "end": v(22.85, -1.94) * mm});
            skLineSegment(sketch, "E94.2.0.36", {"start": v(25.75, 2.29) * mm, "end": v(25.75, 0.69) * mm});
            skLineSegment(sketch, "E94.2.0.37", {"start": v(22.58, -2.5) * mm, "end": v(20.13, -5.54) * mm});
            skLineSegment(sketch, "E94.2.0.38", {"start": v(25.75, -2.29) * mm, "end": v(25.75, -0.69) * mm});
            skCircle(sketch, "E94.2.0.39", {"center": v(19.06, -7.52) * mm, "radius": 2 * mm});
            skLineSegment(sketch, "E94.2.0.40", {"start": v(25.4, 2.8) * mm, "end": v(25.4, 3.92) * mm});
            skPoint(sketch, "E94.2.0.41", {"position": v(22.85, 2.15) * mm});
            skLineSegment(sketch, "E94.2.0.42", {"start": v(27.42, -2.5) * mm, "end": v(29.87, -5.54) * mm});
            skPoint(sketch, "E94.2.0.43", {"position": v(27.15, 2.15) * mm});
            skPoint(sketch, "E94.2.0.44", {"position": v(25, 0) * mm});
            skPoint(sketch, "E94.2.0.45", {"position": v(24.25, 2.5) * mm});
            skPoint(sketch, "E94.2.0.46", {"position": v(24.25, -2.5) * mm});
            skPoint(sketch, "E94.2.0.47", {"position": v(27.15, 2.15) * mm});
            skPoint(sketch, "E94.2.0.48", {"position": v(22.85, 2.15) * mm});
            skPoint(sketch, "E94.2.0.49", {"position": v(22.85, -2.15) * mm});
            skPoint(sketch, "E94.2.0.50", {"position": v(25.25, 0) * mm});
            skPoint(sketch, "E94.2.0.51", {"position": v(27.15, -2.15) * mm});
            skArc(sketch, "E94.2.0.52", {"start": v(29.15, -6.62) * mm, "mid": v(29.19, -6.4) * mm, "end": v(29.12, -6.2) * mm});
            skArc(sketch, "E94.2.0.53", {"start": v(24.6, 3.92) * mm, "mid": v(24.54, 4.14) * mm, "end": v(24.38, 4.3) * mm});
            skPoint(sketch, "E94.2.0.54", {"position": v(22.85, 2.15) * mm});
            skPoint(sketch, "E94.2.0.55", {"position": v(27.15, -2.15) * mm});
            skArc(sketch, "E94.2.0.56", {"start": v(29.28, 6.4) * mm, "mid": v(29.6, 6.02) * mm, "end": v(30.02, 5.74) * mm});
            skArc(sketch, "E94.2.0.57", {"start": v(20.85, -6.62) * mm, "mid": v(20.81, -6.4) * mm, "end": v(20.88, -6.2) * mm});
            skArc(sketch, "E94.2.0.58", {"start": v(29.87, -5.54) * mm, "mid": v(30.05, -5.64) * mm, "end": v(30.25, -5.64) * mm});
            skArc(sketch, "E94.2.0.59", {"start": v(25.62, 4.3) * mm, "mid": v(25.47, 4.14) * mm, "end": v(25.4, 3.92) * mm});
            skArc(sketch, "E94.2.0.60", {"start": v(20.85, 6.62) * mm, "mid": v(20.48, 6.1) * mm, "end": v(19.98, 5.74) * mm});
            skArc(sketch, "E94.2.0.61", {"start": v(20.13, -5.54) * mm, "mid": v(19.95, -5.64) * mm, "end": v(19.75, -5.64) * mm});
            skPoint(sketch, "E94.2.0.62", {"position": v(27.15, 2.15) * mm});
            skArc(sketch, "E94.2.0.63", {"start": v(25.4, -3.92) * mm, "mid": v(25.46, -4.13) * mm, "end": v(25.61, -4.3) * mm});
            skLineSegment(sketch, "E94.2.0.64", {"start": v(24.6, 3.92) * mm, "end": v(24.6, 3) * mm});
            skLineSegment(sketch, "E94.2.0.65", {"start": v(24.6, -3) * mm, "end": v(24.6, -3.92) * mm});
            skPoint(sketch, "E94.2.0.66", {"position": v(22.85, -2.15) * mm});
            skArc(sketch, "E94.2.0.67", {"start": v(30.02, 5.74) * mm, "mid": v(30.14, 5.68) * mm, "end": v(30.27, 5.63) * mm});
            skPoint(sketch, "E94.2.0.68", {"position": v(22.85, -2.15) * mm});
            skPoint(sketch, "E94.2.0.69", {"position": v(27.15, 2.15) * mm});
            skLineSegment(sketch, "E94.2.0.70", {"start": v(25.75, 0) * mm, "end": v(25.75, 0.51) * mm});
            skArc(sketch, "E94.2.0.71", {"start": v(20.85, 6.62) * mm, "mid": v(20.81, 6.4) * mm, "end": v(20.9, 6.19) * mm});
            skArc(sketch, "E94.2.0.72", {"start": v(24.6, -3.92) * mm, "mid": v(24.54, -4.13) * mm, "end": v(24.39, -4.3) * mm});
            skArc(sketch, "E94.2.0.73", {"start": v(25.4, 2.8) * mm, "mid": v(25.49, 2.59) * mm, "end": v(25.7, 2.5) * mm});
            skArc(sketch, "E94.2.0.74", {"start": v(24.34, -0.54) * mm, "mid": v(24.28, -0.56) * mm, "end": v(24.25, -0.51) * mm});
            skArc(sketch, "E94.2.0.75", {"start": v(30.27, 5.63) * mm, "mid": v(30.06, 5.63) * mm, "end": v(29.86, 5.54) * mm});
            skArc(sketch, "E94.2.0.76", {"start": v(25.4, -2.8) * mm, "mid": v(25.49, -2.59) * mm, "end": v(25.7, -2.5) * mm});
            skArc(sketch, "E94.2.0.77", {"start": v(29.12, 6.2) * mm, "mid": v(29.2, 6.4) * mm, "end": v(29.16, 6.6) * mm});
            skArc(sketch, "E94.2.0.78", {"start": v(20.14, 5.54) * mm, "mid": v(19.95, 5.63) * mm, "end": v(19.73, 5.63) * mm});
            skPoint(sketch, "E94.2.0.79", {"position": v(22.85, 2.15) * mm});
            skArc(sketch, "E94.2.0.80", {"start": v(24.34, 0.54) * mm, "mid": v(24.28, 0.56) * mm, "end": v(24.25, 0.51) * mm});
            skArc(sketch, "E94.2.0.81", {"start": v(29.16, 6.6) * mm, "mid": v(29.21, 6.5) * mm, "end": v(29.28, 6.4) * mm});
            skArc(sketch, "E94.2.0.82", {"start": v(19.98, 5.74) * mm, "mid": v(19.86, 5.68) * mm, "end": v(19.73, 5.63) * mm});
            skPoint(sketch, "E94.2.0.83", {"position": v(27.15, -2.15) * mm});
            skLineSegment(sketch, "E94.2.0.84", {"start": v(25.28, 0.04) * mm, "end": v(25.66, 0.54) * mm});
            skLineSegment(sketch, "E94.2.0.85", {"start": v(25.75, 0.69) * mm, "end": v(25.75, 0.51) * mm});
            skArc(sketch, "E94.2.0.86", {"start": v(24.6, 2.8) * mm, "mid": v(24.51, 2.59) * mm, "end": v(24.3, 2.5) * mm});
            skPoint(sketch, "E94.2.0.87", {"position": v(22.85, -2.15) * mm});
            skPoint(sketch, "E94.2.0.88", {"position": v(22.85, 2.15) * mm});
            skLineSegment(sketch, "E94.2.0.89", {"start": v(24.6, 3) * mm, "end": v(24.6, 2.8) * mm});
            skLineSegment(sketch, "E94.2.0.90", {"start": v(24.6, -2.8) * mm, "end": v(24.6, -3) * mm});
            skLineSegment(sketch, "E94.2.0.91", {"start": v(25.75, -0.69) * mm, "end": v(25.75, -0.51) * mm});
            skLineSegment(sketch, "E94.2.0.92", {"start": v(25.75, 0) * mm, "end": v(25.75, -0.51) * mm});
            skPoint(sketch, "E94.2.0.93", {"position": v(27.15, -2.15) * mm});
            skLineSegment(sketch, "E94.2.0.94", {"start": v(24.72, 0.04) * mm, "end": v(24.34, 0.54) * mm});
            skArc(sketch, "E94.2.0.95", {"start": v(25.66, -0.54) * mm, "mid": v(25.72, -0.56) * mm, "end": v(25.75, -0.51) * mm});
            skArc(sketch, "E94.2.0.96", {"start": v(19.9, 2.36) * mm, "mid": v(20.2, 2.22) * mm, "end": v(20.5, 2.15) * mm});
            skLineSegment(sketch, "E94.2.0.97", {"start": v(20.15, 2.15) * mm, "end": v(20.14, 2.15) * mm});
            skPoint(sketch, "E94.2.0.98", {"position": v(27.15, 2.15) * mm});
            skArc(sketch, "E94.2.0.99", {"start": v(24.6, -3.92) * mm, "mid": v(24.54, -4.13) * mm, "end": v(24.39, -4.3) * mm});
            skArc(sketch, "E94.2.0.100", {"start": v(24.6, -2.8) * mm, "mid": v(24.51, -2.59) * mm, "end": v(24.3, -2.5) * mm});
            skPoint(sketch, "E94.2.0.101", {"position": v(22.85, -2.15) * mm});
            skPoint(sketch, "E94.2.0.102", {"position": v(22.85, 2.15) * mm});
            skArc(sketch, "E94.2.0.103", {"start": v(20.09, 2.2) * mm, "mid": v(20, 2.28) * mm, "end": v(19.9, 2.36) * mm});
            skArc(sketch, "E94.2.0.104", {"start": v(23.95, -2.5) * mm, "mid": v(23.86, -2.52) * mm, "end": v(23.79, -2.58) * mm});
            skPoint(sketch, "E94.2.0.105", {"position": v(27.15, -2.15) * mm});
            skArc(sketch, "E94.2.0.106", {"start": v(25.66, 0.54) * mm, "mid": v(25.72, 0.56) * mm, "end": v(25.75, 0.51) * mm});
            skLineSegment(sketch, "E94.2.0.107", {"start": v(24.04, -2.5) * mm, "end": v(23.95, -2.5) * mm});
            skArc(sketch, "E94.2.0.108", {"start": v(27.15, 1.94) * mm, "mid": v(27.22, 2.25) * mm, "end": v(27.42, 2.5) * mm});
            skArc(sketch, "E94.2.0.109", {"start": v(20.15, 2.05) * mm, "mid": v(20.13, 2.13) * mm, "end": v(20.09, 2.2) * mm});
            skArc(sketch, "E94.2.0.110", {"start": v(24.04, -2.5) * mm, "mid": v(24.19, -2.44) * mm, "end": v(24.25, -2.29) * mm});
            skArc(sketch, "E94.2.0.111", {"start": v(26.21, -2.58) * mm, "mid": v(26.14, -2.52) * mm, "end": v(26.05, -2.5) * mm});
            skLineSegment(sketch, "E94.2.0.112", {"start": v(25.96, -2.5) * mm, "end": v(26.05, -2.5) * mm});
            skLineSegment(sketch, "E94.2.0.113", {"start": v(24.04, 2.5) * mm, "end": v(24.25, 2.5) * mm});
            skLineSegment(sketch, "E94.2.0.114", {"start": v(24.04, 2.5) * mm, "end": v(23.95, 2.5) * mm});
            skLineSegment(sketch, "E94.2.0.115", {"start": v(24.25, 2.5) * mm, "end": v(24.3, 2.5) * mm});
            skArc(sketch, "E94.2.0.116", {"start": v(26.05, 2.5) * mm, "mid": v(26.14, 2.52) * mm, "end": v(26.21, 2.58) * mm});
            skLineSegment(sketch, "E94.2.0.117", {"start": v(24.04, -2.5) * mm, "end": v(24.25, -2.5) * mm});
            skLineSegment(sketch, "E94.2.0.118", {"start": v(25.75, 2.5) * mm, "end": v(25.7, 2.5) * mm});
            skPoint(sketch, "E94.2.0.119", {"position": v(22.85, -2.15) * mm});
            skLineSegment(sketch, "E94.2.0.120", {"start": v(25.75, -2.5) * mm, "end": v(25.7, -2.5) * mm});
            skArc(sketch, "E94.2.0.121", {"start": v(24.25, 2.29) * mm, "mid": v(24.19, 2.44) * mm, "end": v(24.04, 2.5) * mm});
            skPoint(sketch, "E94.2.0.122", {"position": v(27.15, -2.15) * mm});
            skLineSegment(sketch, "E94.2.0.123", {"start": v(24.72, -0.04) * mm, "end": v(24.34, -0.54) * mm});
            skArc(sketch, "E94.2.0.124", {"start": v(25.96, 2.5) * mm, "mid": v(25.81, 2.44) * mm, "end": v(25.75, 2.29) * mm});
            skArc(sketch, "E94.2.0.125", {"start": v(24.73, 0) * mm, "mid": v(24.73, -0.02) * mm, "end": v(24.72, -0.04) * mm});
            skArc(sketch, "E94.2.0.126", {"start": v(25.75, -2.29) * mm, "mid": v(25.81, -2.44) * mm, "end": v(25.96, -2.5) * mm});
            skArc(sketch, "E94.2.0.127", {"start": v(23.79, 2.58) * mm, "mid": v(23.86, 2.52) * mm, "end": v(23.95, 2.5) * mm});
            skLineSegment(sketch, "E94.2.0.128", {"start": v(24.25, -2.5) * mm, "end": v(24.3, -2.5) * mm});
            skArc(sketch, "E94.2.0.129", {"start": v(22.85, 1.94) * mm, "mid": v(22.78, 2.25) * mm, "end": v(22.58, 2.5) * mm});
            skLineSegment(sketch, "E94.2.0.130", {"start": v(25.75, 2.5) * mm, "end": v(25.96, 2.5) * mm});
            skLineSegment(sketch, "E94.2.0.131", {"start": v(25.75, -2.5) * mm, "end": v(25.96, -2.5) * mm});
            skArc(sketch, "E94.2.0.132", {"start": v(24.72, 0.04) * mm, "mid": v(24.73, 0.02) * mm, "end": v(24.73, 0) * mm});
            skArc(sketch, "E94.2.0.133", {"start": v(22.58, -2.5) * mm, "mid": v(22.74, -2.23) * mm, "end": v(22.85, -1.94) * mm});
            skLineSegment(sketch, "E94.2.0.134", {"start": v(25.96, 2.5) * mm, "end": v(26.05, 2.5) * mm});
            skArc(sketch, "E94.2.0.135", {"start": v(27.42, -2.5) * mm, "mid": v(27.26, -2.23) * mm, "end": v(27.15, -1.94) * mm});
            skArc(sketch, "E94.2.0.136", {"start": v(25.27, 0) * mm, "mid": v(25.27, -0.02) * mm, "end": v(25.28, -0.04) * mm});
            skLineSegment(sketch, "E94.2.0.137", {"start": v(25.28, -0.04) * mm, "end": v(25.66, -0.54) * mm});
            skArc(sketch, "E94.2.0.138", {"start": v(25.28, 0.04) * mm, "mid": v(25.27, 0.02) * mm, "end": v(25.27, 0) * mm});
            skLineSegment(sketch, "E94.direction1", {"start": v(-32.94, -7.44) * mm, "end": v(-7.94, -7.44) * mm, "construction": true});
            skArc(sketch, "E95.3.0", {"start": v(5.64, 51.28) * mm, "mid": v(9.02, 53.27) * mm, "end": v(6.63, 50.16) * mm});
            skPoint(sketch, "E95.3.1", {"position": v(7.45, 53.95) * mm});
            skPoint(sketch, "E95.3.2", {"position": v(-7.43, 53.95) * mm});
            skPoint(sketch, "E95.3.4", {"position": v(-2.49, 47.16) * mm});
            skPoint(sketch, "E95.3.5", {"position": v(0.01, 45.26) * mm});
            skPoint(sketch, "E95.3.6", {"position": v(2.51, 47.16) * mm});
            skPoint(sketch, "E95.3.7", {"position": v(-5.94, 45.5) * mm});
            skPoint(sketch, "E95.3.8", {"position": v(0.01, 45.76) * mm});
            skLineSegment(sketch, "E95.3.9", {"start": v(-2.48, 48.43) * mm, "end": v(-5.53, 50.88) * mm});
            skLineSegment(sketch, "E95.3.10", {"start": v(-2.57, 47.22) * mm, "end": v(-6.2, 50.13) * mm});
            skCircle(sketch, "E95.3.11", {"center": v(-7.5, 51.95) * mm, "radius": 2 * mm});
            skPoint(sketch, "E95.3.12", {"position": v(-6.08, 46.01) * mm});
            skLineSegment(sketch, "E95.3.13", {"start": v(2.59, 47.22) * mm, "end": v(6.2, 50.11) * mm});
            skLineSegment(sketch, "E95.3.14", {"start": v(2.5, 48.43) * mm, "end": v(5.55, 50.87) * mm});
            skPoint(sketch, "E95.3.15", {"position": v(-2.28, 45.26) * mm});
            skPoint(sketch, "E95.3.16", {"position": v(2.16, 48.16) * mm});
            skPoint(sketch, "E95.3.18", {"position": v(-2.14, 48.16) * mm});
            skPoint(sketch, "E95.3.19", {"position": v(-2.49, 45.26) * mm});
            skPoint(sketch, "E95.3.20", {"position": v(-0.69, 56.16) * mm});
            skPoint(sketch, "E95.3.21", {"position": v(2.51, 46.76) * mm});
            skPoint(sketch, "E95.3.23", {"position": v(6.1, 46.01) * mm});
            skPoint(sketch, "E95.3.25", {"position": v(-2.49, 46.76) * mm});
            skLineSegment(sketch, "E95.3.26", {"start": v(1.95, 48.16) * mm, "end": v(-1.93, 48.16) * mm});
            skPoint(sketch, "E95.3.27", {"position": v(0.01, 46.01) * mm});
            skPoint(sketch, "E95.3.29", {"position": v(-2.49, 46.76) * mm});
            skPoint(sketch, "E95.3.31", {"position": v(2.51, 45.26) * mm});
            skPoint(sketch, "E95.3.32", {"position": v(2.51, 46.76) * mm});
            skArc(sketch, "E95.3.33", {"start": v(4.31, 45.39) * mm, "mid": v(6.1, 46) * mm, "end": v(4.32, 46.63) * mm});
            skArc(sketch, "E95.3.34", {"start": v(-4.29, 46.63) * mm, "mid": v(-6.08, 46.01) * mm, "end": v(-4.29, 45.4) * mm});
            skPoint(sketch, "E95.3.35", {"position": v(2.16, 48.16) * mm});
            skPoint(sketch, "E95.3.36", {"position": v(-2.14, 48.16) * mm});
            skLineSegment(sketch, "E95.3.38", {"start": v(5.1, 46.01) * mm, "end": v(-5.08, 46.01) * mm});
            skArc(sketch, "E95.3.40", {"start": v(-6.6, 50.16) * mm, "mid": v(-6.4, 50.2) * mm, "end": v(-6.2, 50.13) * mm});
            skPoint(sketch, "E95.3.41", {"position": v(2.16, 48.16) * mm});
            skPoint(sketch, "E95.3.43", {"position": v(-2.14, 48.16) * mm});
            skArc(sketch, "E95.3.44", {"start": v(-5.53, 50.88) * mm, "mid": v(-5.63, 51.06) * mm, "end": v(-5.63, 51.26) * mm});
            skArc(sketch, "E95.3.45", {"start": v(3.93, 46.41) * mm, "mid": v(4.15, 46.47) * mm, "end": v(4.32, 46.63) * mm});
            skPoint(sketch, "E95.3.46", {"position": v(2.16, 48.16) * mm});
            skPoint(sketch, "E95.3.48", {"position": v(-2.14, 48.16) * mm});
            skArc(sketch, "E95.3.52", {"start": v(-3.9, 46.41) * mm, "mid": v(-4.12, 46.48) * mm, "end": v(-4.29, 46.63) * mm});
            skPoint(sketch, "E95.3.53", {"position": v(-2.14, 48.16) * mm});
            skPoint(sketch, "E95.3.54", {"position": v(2.16, 48.16) * mm});
            skArc(sketch, "E95.3.57", {"start": v(6.63, 50.16) * mm, "mid": v(6.12, 50.53) * mm, "end": v(5.75, 51.03) * mm});
            skPoint(sketch, "E95.3.58", {"position": v(2.16, 48.16) * mm});
            skPoint(sketch, "E95.3.59", {"position": v(-2.14, 48.16) * mm});
            skArc(sketch, "E95.3.60", {"start": v(2.06, 50.86) * mm, "mid": v(2.15, 50.88) * mm, "end": v(2.21, 50.93) * mm});
            skArc(sketch, "E95.3.62", {"start": v(-3.9, 46.41) * mm, "mid": v(-4.12, 46.48) * mm, "end": v(-4.29, 46.63) * mm});
            skArc(sketch, "E95.3.63", {"start": v(6.63, 50.16) * mm, "mid": v(6.4, 50.2) * mm, "end": v(6.2, 50.11) * mm});
            skArc(sketch, "E95.3.64", {"start": v(5.75, 51.03) * mm, "mid": v(5.7, 51.15) * mm, "end": v(5.64, 51.28) * mm});
            skLineSegment(sketch, "E95.3.65", {"start": v(-2.28, 46.76) * mm, "end": v(2.3, 46.76) * mm});
            skArc(sketch, "E95.3.66", {"start": v(2.37, 51.1) * mm, "mid": v(2.23, 50.82) * mm, "end": v(2.16, 50.51) * mm});
            skArc(sketch, "E95.3.67", {"start": v(5.55, 50.87) * mm, "mid": v(5.64, 51.06) * mm, "end": v(5.64, 51.28) * mm});
            skLineSegment(sketch, "E95.3.68", {"start": v(2.16, 50.86) * mm, "end": v(2.16, 50.87) * mm});
            skPoint(sketch, "E95.3.69", {"position": v(-2.14, 48.16) * mm});
            skLineSegment(sketch, "E95.3.71", {"start": v(3.93, 46.41) * mm, "end": v(3, 46.41) * mm});
            skArc(sketch, "E95.3.73", {"start": v(2.21, 50.93) * mm, "mid": v(2.3, 51.01) * mm, "end": v(2.37, 51.1) * mm});
            skLineSegment(sketch, "E95.3.75", {"start": v(-2.98, 46.41) * mm, "end": v(-3.9, 46.41) * mm});
            skArc(sketch, "E95.3.76", {"start": v(1.95, 48.16) * mm, "mid": v(2.26, 48.23) * mm, "end": v(2.5, 48.43) * mm});
            skArc(sketch, "E95.3.78", {"start": v(-2.48, 48.43) * mm, "mid": v(-2.22, 48.27) * mm, "end": v(-1.93, 48.16) * mm});
            skLineSegment(sketch, "E95.3.79", {"start": v(-0.03, 46.3) * mm, "end": v(-0.53, 46.67) * mm});
            skLineSegment(sketch, "E95.3.80", {"start": v(0.06, 46.3) * mm, "end": v(0.55, 46.67) * mm});
            skLineSegment(sketch, "E95.3.82", {"start": v(0.01, 45.26) * mm, "end": v(-0.5, 45.26) * mm});
            skLineSegment(sketch, "E95.3.83", {"start": v(2.3, 45.26) * mm, "end": v(0.7, 45.26) * mm});
            skLineSegment(sketch, "E95.3.86", {"start": v(0.01, 45.26) * mm, "end": v(0.52, 45.26) * mm});
            skLineSegment(sketch, "E95.3.87", {"start": v(-2.28, 45.26) * mm, "end": v(-0.68, 45.26) * mm});
            skArc(sketch, "E95.3.89", {"start": v(0.01, 46.28) * mm, "mid": v(-0.01, 46.28) * mm, "end": v(-0.03, 46.3) * mm});
            skArc(sketch, "E95.3.91", {"start": v(2.51, 44.96) * mm, "mid": v(2.53, 44.87) * mm, "end": v(2.59, 44.8) * mm});
            skArc(sketch, "E95.3.92", {"start": v(0.06, 46.3) * mm, "mid": v(0.03, 46.28) * mm, "end": v(0.01, 46.28) * mm});
            skArc(sketch, "E95.3.94", {"start": v(2.81, 45.61) * mm, "mid": v(2.6, 45.52) * mm, "end": v(2.51, 45.31) * mm});
            skArc(sketch, "E95.3.97", {"start": v(-0.53, 46.67) * mm, "mid": v(-0.55, 46.73) * mm, "end": v(-0.5, 46.76) * mm});
            skArc(sketch, "E95.3.100", {"start": v(2.51, 45.05) * mm, "mid": v(2.45, 45.2) * mm, "end": v(2.3, 45.26) * mm});
            skLineSegment(sketch, "E95.3.101", {"start": v(0.7, 45.26) * mm, "end": v(0.52, 45.26) * mm});
            skArc(sketch, "E95.3.102", {"start": v(0.55, 46.67) * mm, "mid": v(0.57, 46.73) * mm, "end": v(0.52, 46.76) * mm});
            skLineSegment(sketch, "E95.3.103", {"start": v(-2.49, 46.97) * mm, "end": v(-2.49, 47.06) * mm});
            skLineSegment(sketch, "E95.3.104", {"start": v(2.51, 45.26) * mm, "end": v(2.51, 45.05) * mm});
            skArc(sketch, "E95.3.106", {"start": v(-2.49, 47.06) * mm, "mid": v(-2.51, 47.15) * mm, "end": v(-2.57, 47.22) * mm});
            skLineSegment(sketch, "E95.3.107", {"start": v(2.51, 45.05) * mm, "end": v(2.51, 44.96) * mm});
            skLineSegment(sketch, "E95.3.108", {"start": v(-0.68, 45.26) * mm, "end": v(-0.5, 45.26) * mm});
            skLineSegment(sketch, "E95.3.109", {"start": v(2.51, 45.26) * mm, "end": v(2.51, 45.31) * mm});
            skLineSegment(sketch, "E95.3.110", {"start": v(-2.49, 45.26) * mm, "end": v(-2.49, 45.31) * mm});
            skLineSegment(sketch, "E95.3.112", {"start": v(-2.79, 46.41) * mm, "end": v(-2.98, 46.41) * mm});
            skArc(sketch, "E95.3.113", {"start": v(-2.79, 46.41) * mm, "mid": v(-2.58, 46.5) * mm, "end": v(-2.49, 46.71) * mm});
            skLineSegment(sketch, "E95.3.114", {"start": v(3, 46.41) * mm, "end": v(2.81, 46.41) * mm});
            skLineSegment(sketch, "E95.3.115", {"start": v(2.51, 46.97) * mm, "end": v(2.51, 46.76) * mm});
            skArc(sketch, "E95.3.116", {"start": v(2.3, 46.76) * mm, "mid": v(2.45, 46.82) * mm, "end": v(2.51, 46.97) * mm});
            skLineSegment(sketch, "E95.3.117", {"start": v(-2.49, 46.97) * mm, "end": v(-2.49, 46.76) * mm});
            skLineSegment(sketch, "E95.3.118", {"start": v(-2.49, 46.76) * mm, "end": v(-2.49, 46.71) * mm});
            skArc(sketch, "E95.3.119", {"start": v(2.81, 46.41) * mm, "mid": v(2.6, 46.5) * mm, "end": v(2.51, 46.71) * mm});
            skArc(sketch, "E95.3.120", {"start": v(2.59, 47.22) * mm, "mid": v(2.53, 47.15) * mm, "end": v(2.51, 47.06) * mm});
            skLineSegment(sketch, "E95.3.121", {"start": v(2.51, 46.97) * mm, "end": v(2.51, 47.06) * mm});
            skLineSegment(sketch, "E95.3.122", {"start": v(2.51, 46.76) * mm, "end": v(2.51, 46.71) * mm});
            skArc(sketch, "E95.3.123", {"start": v(-2.49, 46.97) * mm, "mid": v(-2.43, 46.82) * mm, "end": v(-2.28, 46.76) * mm});
            skLineSegment(sketch, "E96", {"start": v(2.3, 45.26) * mm, "end": v(4.44, 45.26) * mm});
            skLineSegment(sketch, "E97", {"start": v(-2.28, 45.26) * mm, "end": v(-4.41, 45.26) * mm});
            skLineSegment(sketch, "E98.bottom", {"start": v(12.5, 41.3) * mm, "end": v(-12.5, 41.3) * mm});
            skLineSegment(sketch, "E98.top", {"start": v(12.5, 57.3) * mm, "end": v(-12.5, 57.3) * mm});
            skLineSegment(sketch, "E98.left", {"start": v(12.5, 41.3) * mm, "end": v(12.5, 57.3) * mm});
            skLineSegment(sketch, "E98.right", {"start": v(-12.5, 41.3) * mm, "end": v(-12.5, 57.3) * mm});
            skPoint(sketch, "E98.middle", {"position": v(0, 49.3) * mm});
            skLineSegment(sketch, "E99.1.0.0", {"start": v(12.46, -30.01) * mm, "end": v(-12.54, -30.01) * mm});
            skLineSegment(sketch, "E99.1.0.1", {"start": v(12.46, -30.01) * mm, "end": v(12.46, -14.01) * mm});
            skLineSegment(sketch, "E99.1.0.2", {"start": v(2.46, -22.88) * mm, "end": v(5.51, -20.44) * mm});
            skPoint(sketch, "E99.1.0.3", {"position": v(-0.03, -25.3) * mm});
            skPoint(sketch, "E99.1.0.4", {"position": v(2.47, -24.55) * mm});
            skPoint(sketch, "E99.1.0.5", {"position": v(-6.11, -25.3) * mm});
            skPoint(sketch, "E99.1.0.6", {"position": v(6.06, -25.3) * mm});
            skCircle(sketch, "E99.1.0.7", {"center": v(-7.54, -19.36) * mm, "radius": 2 * mm});
            skLineSegment(sketch, "E99.1.0.8", {"start": v(2.55, -24.09) * mm, "end": v(6.16, -21.2) * mm});
            skLineSegment(sketch, "E99.1.0.9", {"start": v(-2.6, -24.09) * mm, "end": v(-6.23, -21.18) * mm});
            skLineSegment(sketch, "E99.1.0.10", {"start": v(-2.52, -22.88) * mm, "end": v(-5.57, -20.43) * mm});
            skArc(sketch, "E99.1.0.11", {"start": v(5.6, -20.03) * mm, "mid": v(8.99, -18.04) * mm, "end": v(6.59, -21.15) * mm});
            skPoint(sketch, "E99.1.0.12", {"position": v(2.47, -24.15) * mm});
            skPoint(sketch, "E99.1.0.13", {"position": v(-0.04, -22.01) * mm});
            skPoint(sketch, "E99.1.0.14", {"position": v(-0.73, -15.15) * mm});
            skPoint(sketch, "E99.1.0.15", {"position": v(7.41, -17.36) * mm});
            skPoint(sketch, "E99.1.0.16", {"position": v(2.12, -23.15) * mm});
            skPoint(sketch, "E99.1.0.17", {"position": v(-0.03, -26.05) * mm});
            skPoint(sketch, "E99.1.0.18", {"position": v(-7.46, -17.36) * mm});
            skPoint(sketch, "E99.1.0.19", {"position": v(-2.17, -23.15) * mm});
            skPoint(sketch, "E99.1.0.20", {"position": v(-2.53, -26.05) * mm});
            skPoint(sketch, "E99.1.0.21", {"position": v(2.47, -26.05) * mm});
            skPoint(sketch, "E99.1.0.22", {"position": v(-5.97, -25.81) * mm});
            skPoint(sketch, "E99.1.0.23", {"position": v(2.12, -23.15) * mm});
            skPoint(sketch, "E99.1.0.24", {"position": v(2.47, -24.55) * mm});
            skArc(sketch, "E99.1.0.25", {"start": v(4.28, -25.92) * mm, "mid": v(6.06, -25.3) * mm, "end": v(4.28, -24.68) * mm});
            skLineSegment(sketch, "E99.1.0.26", {"start": v(2.26, -26.05) * mm, "end": v(4.4, -26.05) * mm});
            skArc(sketch, "E99.1.0.27", {"start": v(-4.32, -24.68) * mm, "mid": v(-6.11, -25.3) * mm, "end": v(-4.32, -25.91) * mm});
            skPoint(sketch, "E99.1.0.28", {"position": v(-2.32, -26.05) * mm});
            skPoint(sketch, "E99.1.0.29", {"position": v(-2.53, -24.55) * mm});
            skPoint(sketch, "E99.1.0.30", {"position": v(-2.53, -24.15) * mm});
            skLineSegment(sketch, "E99.1.0.31", {"start": v(1.91, -23.15) * mm, "end": v(-1.96, -23.15) * mm});
            skPoint(sketch, "E99.1.0.32", {"position": v(-0.03, -25.55) * mm});
            skPoint(sketch, "E99.1.0.33", {"position": v(-2.17, -23.15) * mm});
            skPoint(sketch, "E99.1.0.34", {"position": v(-2.17, -23.15) * mm});
            skPoint(sketch, "E99.1.0.35", {"position": v(2.12, -23.15) * mm});
            skPoint(sketch, "E99.1.0.36", {"position": v(-2.53, -24.55) * mm});
            skLineSegment(sketch, "E99.1.0.37", {"start": v(5.06, -25.3) * mm, "end": v(-5.11, -25.3) * mm});
            skArc(sketch, "E99.1.0.38", {"start": v(-5.57, -20.43) * mm, "mid": v(-5.67, -20.25) * mm, "end": v(-5.66, -20.05) * mm});
            skArc(sketch, "E99.1.0.39", {"start": v(3.9, -24.9) * mm, "mid": v(4.12, -24.84) * mm, "end": v(4.28, -24.68) * mm});
            skArc(sketch, "E99.1.0.40", {"start": v(-6.64, -21.15) * mm, "mid": v(-6.43, -21.11) * mm, "end": v(-6.23, -21.18) * mm});
            skPoint(sketch, "E99.1.0.41", {"position": v(2.12, -23.15) * mm});
            skArc(sketch, "E99.1.0.42", {"start": v(-3.95, -24.9) * mm, "mid": v(-4.16, -24.84) * mm, "end": v(-4.32, -24.68) * mm});
            skPoint(sketch, "E99.1.0.43", {"position": v(-2.17, -23.15) * mm});
            skLineSegment(sketch, "E99.1.0.44", {"start": v(3.9, -24.9) * mm, "end": v(2.97, -24.9) * mm});
            skArc(sketch, "E99.1.0.45", {"start": v(5.51, -20.44) * mm, "mid": v(5.6, -20.25) * mm, "end": v(5.6, -20.03) * mm});
            skArc(sketch, "E99.1.0.46", {"start": v(2.33, -20.2) * mm, "mid": v(2.2, -20.5) * mm, "end": v(2.12, -20.8) * mm});
            skArc(sketch, "E99.1.0.47", {"start": v(2.18, -20.39) * mm, "mid": v(2.26, -20.3) * mm, "end": v(2.33, -20.2) * mm});
            skPoint(sketch, "E99.1.0.48", {"position": v(2.12, -23.15) * mm});
            skArc(sketch, "E99.1.0.49", {"start": v(-3.95, -24.9) * mm, "mid": v(-4.16, -24.84) * mm, "end": v(-4.32, -24.68) * mm});
            skPoint(sketch, "E99.1.0.50", {"position": v(-2.17, -23.15) * mm});
            skArc(sketch, "E99.1.0.51", {"start": v(6.59, -21.15) * mm, "mid": v(6.08, -20.78) * mm, "end": v(5.71, -20.28) * mm});
            skArc(sketch, "E99.1.0.52", {"start": v(6.59, -21.15) * mm, "mid": v(6.37, -21.11) * mm, "end": v(6.16, -21.2) * mm});
            skArc(sketch, "E99.1.0.53", {"start": v(5.71, -20.28) * mm, "mid": v(5.65, -20.16) * mm, "end": v(5.6, -20.03) * mm});
            skLineSegment(sketch, "E99.1.0.54", {"start": v(2.12, -20.45) * mm, "end": v(2.12, -20.44) * mm});
            skLineSegment(sketch, "E99.1.0.55", {"start": v(2.26, -26.05) * mm, "end": v(0.66, -26.05) * mm});
            skPoint(sketch, "E99.1.0.56", {"position": v(-2.17, -23.15) * mm});
            skPoint(sketch, "E99.1.0.57", {"position": v(2.12, -23.15) * mm});
            skLineSegment(sketch, "E99.1.0.58", {"start": v(-3.02, -24.9) * mm, "end": v(-3.95, -24.9) * mm});
            skArc(sketch, "E99.1.0.59", {"start": v(2.03, -20.45) * mm, "mid": v(2.1, -20.43) * mm, "end": v(2.18, -20.39) * mm});
            skLineSegment(sketch, "E99.1.0.60", {"start": v(-0.03, -26.05) * mm, "end": v(-0.54, -26.05) * mm});
            skLineSegment(sketch, "E99.1.0.61", {"start": v(-2.32, -24.55) * mm, "end": v(2.26, -24.55) * mm});
            skLineSegment(sketch, "E99.1.0.62", {"start": v(-2.32, -26.05) * mm, "end": v(-0.71, -26.05) * mm});
            skLineSegment(sketch, "E99.1.0.63", {"start": v(-0.03, -26.05) * mm, "end": v(0.49, -26.05) * mm});
            skLineSegment(sketch, "E99.1.0.64", {"start": v(-2.53, -26.05) * mm, "end": v(-2.53, -26) * mm});
            skPoint(sketch, "E99.1.0.65", {"position": v(-2.17, -23.15) * mm});
            skArc(sketch, "E99.1.0.66", {"start": v(0.02, -25.02) * mm, "mid": v(0, -25.03) * mm, "end": v(-0.03, -25.03) * mm});
            skLineSegment(sketch, "E99.1.0.67", {"start": v(-0.71, -26.05) * mm, "end": v(-0.54, -26.05) * mm});
            skArc(sketch, "E99.1.0.68", {"start": v(-0.57, -24.64) * mm, "mid": v(-0.59, -24.58) * mm, "end": v(-0.54, -24.55) * mm});
            skLineSegment(sketch, "E99.1.0.69", {"start": v(0.66, -26.05) * mm, "end": v(0.49, -26.05) * mm});
            skLineSegment(sketch, "E99.1.0.70", {"start": v(-0.07, -25.02) * mm, "end": v(-0.57, -24.64) * mm});
            skArc(sketch, "E99.1.0.71", {"start": v(1.91, -23.15) * mm, "mid": v(2.22, -23.08) * mm, "end": v(2.46, -22.88) * mm});
            skLineSegment(sketch, "E99.1.0.72", {"start": v(0.02, -25.02) * mm, "end": v(0.52, -24.64) * mm});
            skArc(sketch, "E99.1.0.73", {"start": v(0.52, -24.64) * mm, "mid": v(0.53, -24.58) * mm, "end": v(0.49, -24.55) * mm});
            skArc(sketch, "E99.1.0.74", {"start": v(-2.52, -22.88) * mm, "mid": v(-2.26, -23.04) * mm, "end": v(-1.96, -23.15) * mm});
            skArc(sketch, "E99.1.0.75", {"start": v(-0.03, -25.03) * mm, "mid": v(-0.05, -25.03) * mm, "end": v(-0.07, -25.02) * mm});
            skArc(sketch, "E99.1.0.76", {"start": v(-2.83, -24.9) * mm, "mid": v(-2.61, -24.81) * mm, "end": v(-2.53, -24.6) * mm});
            skLineSegment(sketch, "E99.1.0.77", {"start": v(-2.53, -24.55) * mm, "end": v(-2.53, -24.6) * mm});
            skArc(sketch, "E99.1.0.78", {"start": v(-2.53, -24.25) * mm, "mid": v(-2.55, -24.16) * mm, "end": v(-2.6, -24.09) * mm});
            skLineSegment(sketch, "E99.1.0.79", {"start": v(-2.83, -24.9) * mm, "end": v(-3.02, -24.9) * mm});
            skLineSegment(sketch, "E99.1.0.80", {"start": v(-2.53, -24.34) * mm, "end": v(-2.53, -24.55) * mm});
            skLineSegment(sketch, "E99.1.0.81", {"start": v(-2.53, -24.34) * mm, "end": v(-2.53, -24.25) * mm});
            skArc(sketch, "E99.1.0.82", {"start": v(2.47, -26.26) * mm, "mid": v(2.41, -26.11) * mm, "end": v(2.26, -26.05) * mm});
            skArc(sketch, "E99.1.0.83", {"start": v(2.47, -26.35) * mm, "mid": v(2.5, -26.44) * mm, "end": v(2.55, -26.51) * mm});
            skArc(sketch, "E99.1.0.84", {"start": v(2.77, -25.7) * mm, "mid": v(2.56, -25.79) * mm, "end": v(2.47, -26) * mm});
            skLineSegment(sketch, "E99.1.0.85", {"start": v(2.97, -24.9) * mm, "end": v(2.77, -24.9) * mm});
            skArc(sketch, "E99.1.0.86", {"start": v(2.77, -24.9) * mm, "mid": v(2.56, -24.81) * mm, "end": v(2.47, -24.6) * mm});
            skLineSegment(sketch, "E99.1.0.87", {"start": v(2.47, -24.34) * mm, "end": v(2.47, -24.25) * mm});
            skArc(sketch, "E99.1.0.88", {"start": v(2.26, -24.55) * mm, "mid": v(2.41, -24.49) * mm, "end": v(2.47, -24.34) * mm});
            skLineSegment(sketch, "E99.1.0.89", {"start": v(2.47, -24.34) * mm, "end": v(2.47, -24.55) * mm});
            skLineSegment(sketch, "E99.1.0.90", {"start": v(2.47, -26.26) * mm, "end": v(2.47, -26.35) * mm});
            skLineSegment(sketch, "E99.1.0.91", {"start": v(2.47, -26.05) * mm, "end": v(2.47, -26) * mm});
            skArc(sketch, "E99.1.0.92", {"start": v(2.55, -24.09) * mm, "mid": v(2.5, -24.16) * mm, "end": v(2.47, -24.25) * mm});
            skLineSegment(sketch, "E99.1.0.93", {"start": v(2.47, -26.05) * mm, "end": v(2.47, -26.26) * mm});
            skLineSegment(sketch, "E99.1.0.94", {"start": v(2.47, -24.55) * mm, "end": v(2.47, -24.6) * mm});
            skLineSegment(sketch, "E99.direction1", {"start": v(-12.5, 41.3) * mm, "end": v(-62.5, 41.3) * mm, "construction": true});
            skLineSegment(sketch, "E100", {"start": v(12.46, -14.01) * mm, "end": v(-14.1, -14.01) * mm});
            skLineSegment(sketch, "E101", {"start": v(-12.54, -30.01) * mm, "end": v(-12.54, -14.01) * mm});
            skLineSegment(sketch, "E102", {"start": v(-2.32, -26.05) * mm, "end": v(-4.45, -26.05) * mm});
            skLineSegment(sketch, "E103", {"start": v(-2.32, -24.55) * mm, "end": v(-2.53, -24.55) * mm});
            skSolve(sketch);
        }
        {
            var Q0;
            {var subQ4=sQuery(id+"F0.wireOp",EDGE,"E93.0.1.57");Q0=makeQuery(id+"F0.imprint","IMPRINT",FACE,{"disambiguationData":[TD([[makeQuery(id+"F0.imprint","IMPRINT",EDGE,{"derivedFrom":subQ4}),1.0]])]});}
            var Q1;
            Q1=makeQuery(id+"F0.imprint","IMPRINT",FACE,{"disambiguationData":[TD([[makeQuery(id+"F0.imprint","IMPRINT",EDGE,{"derivedFrom":sQuery(id+"F0.wireOp",EDGE,"E93.0.1.12")}),-1.0]])]});
            var Q2;
            {var subQ0=sQuery(id+"F0.wireOp",EDGE,"E93.0.1.17");var subQ1=makeQuery(id+"F0.imprint","INTERSECT",VERTEX,{"derivedFrom":[subQ0,sQuery(id+"F0.wireOp",EDGE,"E93.0.1.57")]});Q2=makeQuery(id+"F0.imprint","IMPRINT",FACE,{"disambiguationData":[TD([[makeQuery(id+"F0.imprint","IMPRINT",EDGE,{"disambiguationData":[TD([[subQ1,-1.0]])],"derivedFrom":subQ0}),1.0]])]});}
            extrude(context, id + "F1", {"entities" : qUnion([Q0, Q1, Q2]), "depth" : 1.5 * mm});
        }
        {
            var Q0;
            {var subQ5=sQuery(id+"F0.wireOp",EDGE,"E93.0.1.42");Q0=makeQuery(id+"F0.imprint","IMPRINT",FACE,{"disambiguationData":[TD([[makeQuery(id+"F0.imprint","IMPRINT",EDGE,{"derivedFrom":subQ5}),-1.0]])]});}
            var Q1;
            {var subQ4=sQuery(id+"F0.wireOp",EDGE,"E93.0.1.2");Q1=makeQuery(id+"F0.imprint","IMPRINT",FACE,{"disambiguationData":[TD([[makeQuery(id+"F0.imprint","IMPRINT",EDGE,{"derivedFrom":subQ4}),1.0]])]});}
            var Q2;
            {var subQ0=sQuery(id+"F0.wireOp",EDGE,"E93.0.1.5");var subQ1=makeQuery(id+"F0.imprint","INTERSECT",VERTEX,{"derivedFrom":[subQ0,sQuery(id+"F0.wireOp",EDGE,"E93.0.1.42")]});Q2=makeQuery(id+"F0.imprint","IMPRINT",FACE,{"disambiguationData":[TD([[makeQuery(id+"F0.imprint","IMPRINT",EDGE,{"disambiguationData":[TD([[subQ1,1.0]])],"derivedFrom":subQ0}),-1.0]])]});}
            extrude(context, id + "F2", {"entities" : qUnion([Q0, Q1, Q2]), "depth" : 1.5 * mm});
        }
        {
            var Q0;
            Q0=makeQuery(id+"F0.imprint","IMPRINT",FACE,{"disambiguationData":[TD([[makeQuery(id+"F0.imprint","IMPRINT",EDGE,{"derivedFrom":sQuery(id+"F0.wireOp",EDGE,"E93.0.1.49")}),1.0]])]});
            extrude(context, id + "F3", {"entities" : qUnion([Q0]), "depth" : 1 * mm});
        }
    });
